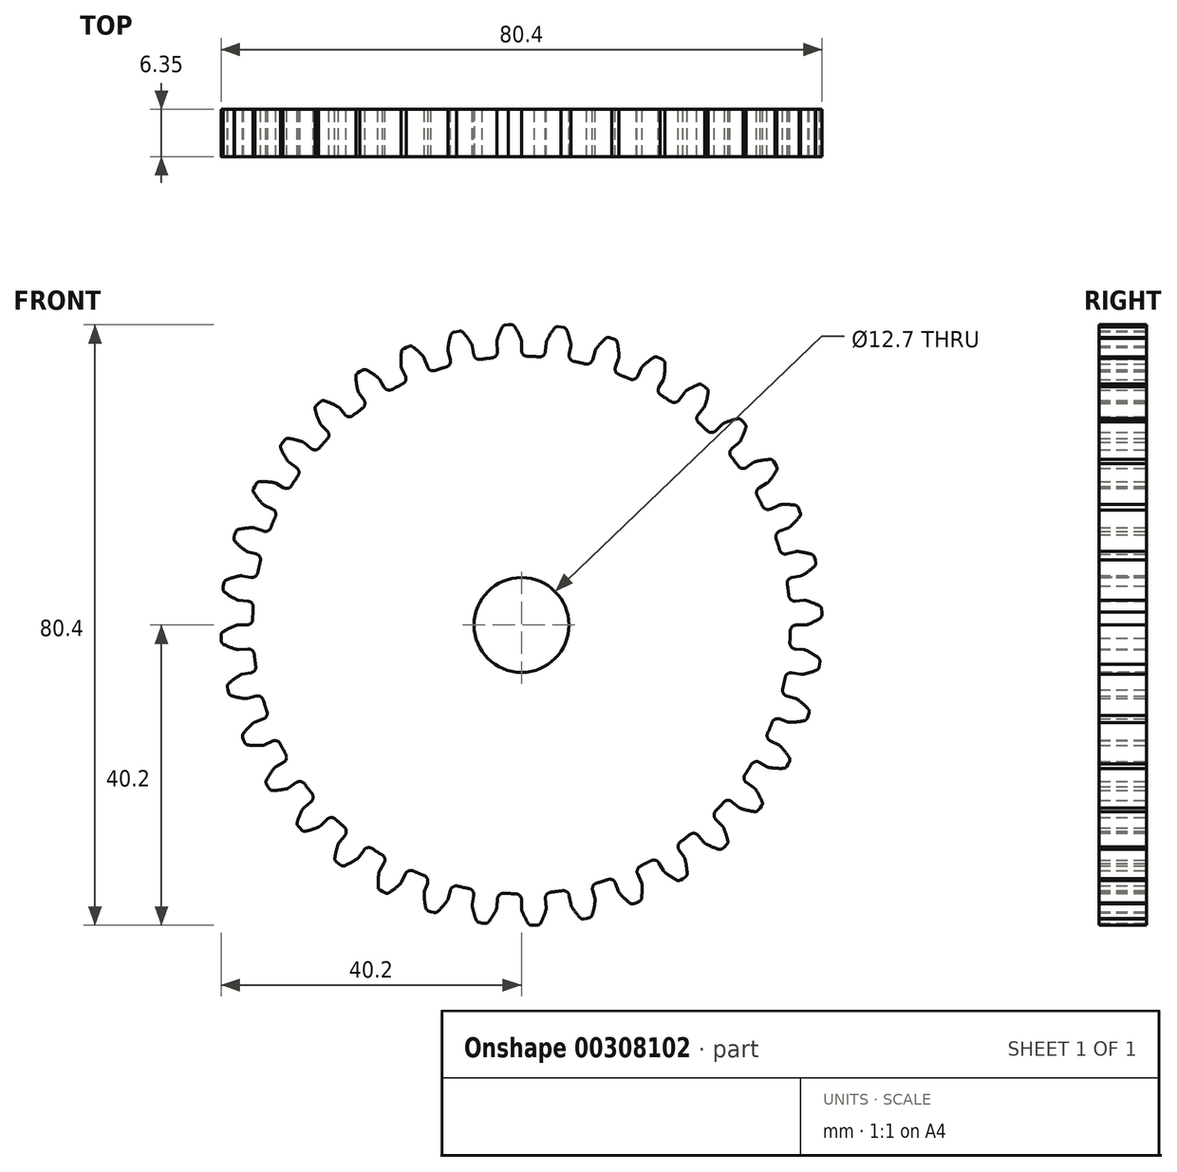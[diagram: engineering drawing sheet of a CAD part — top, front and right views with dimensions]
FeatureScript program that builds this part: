
annotation { "Feature Type Name" : "Feature", "Feature Type Description" : "" }
export const myFeature = defineFeature(function(context is Context, id is Id, definition is map)
    precondition{}
    {
        {
            var Q0;
            Q0=qCreatedBy(makeId("Front.planeOp"),FACE);
            var sketch = newSketch(context, id + "F0", { "sketchPlane" : qUnion([Q0])});
            skArc(sketch, "E0", {"start": v(-3.92, 35.77) * mm, "mid": v(-4.7, 35.68) * mm, "end": v(-5.48, 35.56) * mm});
            skArc(sketch, "E1.trimOffspring", {"start": v(-0.05, 38.24) * mm, "mid": v(-0.44, 39.13) * mm, "end": v(-0.92, 39.97) * mm});
            skLineSegment(sketch, "E2", {"start": v(0, 37.96) * mm, "end": v(0, 36.77) * mm});
            skLineSegment(sketch, "E3", {"start": v(-1.35, 40.2) * mm, "end": v(-1.76, 40.2) * mm});
            skLineSegment(sketch, "E4.MirrorCS", {"start": v(-2.16, 40.17) * mm, "end": v(-1.76, 40.2) * mm});
            skArc(sketch, "E5.MirrorCS", {"start": v(-3.28, 38.1) * mm, "mid": v(-2.97, 39.02) * mm, "end": v(-2.56, 39.9) * mm});
            skLineSegment(sketch, "E6.MirrorCS", {"start": v(-3.3, 37.81) * mm, "end": v(-3.2, 36.63) * mm});
            skPoint(sketch, "E7.visualSharp", {"position": v(-3.14, 35.85) * mm});
            skArc(sketch, "E7.filletArc", {"start": v(-3.92, 35.77) * mm, "mid": v(-3.38, 36.06) * mm, "end": v(-3.2, 36.63) * mm});
            skPoint(sketch, "E8.visualSharp", {"position": v(0, 35.98) * mm});
            skArc(sketch, "E8.filletArc", {"start": v(0, 36.77) * mm, "mid": v(0.23, 36.22) * mm, "end": v(0.78, 35.97) * mm});
            skPoint(sketch, "E9.visualSharp", {"position": v(-3.32, 37.96) * mm});
            skArc(sketch, "E9.filletArc", {"start": v(-3.28, 38.1) * mm, "mid": v(-3.3, 37.96) * mm, "end": v(-3.3, 37.81) * mm});
            skPoint(sketch, "E10.visualSharp", {"position": v(0, 38.1) * mm});
            skArc(sketch, "E10.filletArc", {"start": v(0, 37.96) * mm, "mid": v(-0.01, 38.1) * mm, "end": v(-0.05, 38.24) * mm});
            skPoint(sketch, "E11.visualSharp", {"position": v(-1.08, 40.2) * mm});
            skArc(sketch, "E11.filletArc", {"start": v(-0.92, 39.97) * mm, "mid": v(-1.1, 40.14) * mm, "end": v(-1.35, 40.2) * mm});
            skPoint(sketch, "E12.visualSharp", {"position": v(-2.43, 40.14) * mm});
            skArc(sketch, "E12.filletArc", {"start": v(-2.16, 40.17) * mm, "mid": v(-2.4, 40.08) * mm, "end": v(-2.56, 39.9) * mm});
            skArc(sketch, "E13.1.0", {"start": v(-10.07, 34.55) * mm, "mid": v(-9.6, 34.92) * mm, "end": v(-9.52, 35.52) * mm});
            skLineSegment(sketch, "E13.1.1", {"start": v(-9.82, 36.66) * mm, "end": v(-9.52, 35.52) * mm});
            skArc(sketch, "E13.1.2", {"start": v(-9.85, 36.95) * mm, "mid": v(-9.85, 36.8) * mm, "end": v(-9.82, 36.66) * mm});
            skArc(sketch, "E13.1.3", {"start": v(-9.85, 36.95) * mm, "mid": v(-9.7, 37.9) * mm, "end": v(-9.45, 38.84) * mm});
            skArc(sketch, "E13.1.4", {"start": v(-9.1, 39.18) * mm, "mid": v(-9.32, 39.06) * mm, "end": v(-9.45, 38.84) * mm});
            skLineSegment(sketch, "E13.1.5", {"start": v(-9.1, 39.18) * mm, "end": v(-8.7, 39.29) * mm});
            skLineSegment(sketch, "E13.1.6", {"start": v(-8.31, 39.36) * mm, "end": v(-8.7, 39.29) * mm});
            skArc(sketch, "E13.1.7", {"start": v(-7.85, 39.2) * mm, "mid": v(-8.06, 39.34) * mm, "end": v(-8.31, 39.36) * mm});
            skArc(sketch, "E13.1.8", {"start": v(-6.7, 37.65) * mm, "mid": v(-7.23, 38.46) * mm, "end": v(-7.85, 39.2) * mm});
            skArc(sketch, "E13.1.9", {"start": v(-6.6, 37.38) * mm, "mid": v(-6.63, 37.52) * mm, "end": v(-6.7, 37.65) * mm});
            skLineSegment(sketch, "E13.1.10", {"start": v(-6.6, 37.38) * mm, "end": v(-6.39, 36.22) * mm});
            skArc(sketch, "E13.1.11", {"start": v(-6.39, 36.22) * mm, "mid": v(-6.06, 35.7) * mm, "end": v(-5.48, 35.56) * mm});
            skArc(sketch, "E13.2.0", {"start": v(-15.91, 32.27) * mm, "mid": v(-15.51, 32.73) * mm, "end": v(-15.54, 33.33) * mm});
            skLineSegment(sketch, "E13.2.1", {"start": v(-16.04, 34.4) * mm, "end": v(-15.54, 33.33) * mm});
            skArc(sketch, "E13.2.2", {"start": v(-16.11, 34.68) * mm, "mid": v(-16.1, 34.54) * mm, "end": v(-16.04, 34.4) * mm});
            skArc(sketch, "E13.2.3", {"start": v(-16.11, 34.68) * mm, "mid": v(-16.13, 35.65) * mm, "end": v(-16.05, 36.61) * mm});
            skArc(sketch, "E13.2.4", {"start": v(-15.77, 37) * mm, "mid": v(-15.96, 36.85) * mm, "end": v(-16.05, 36.61) * mm});
            skLineSegment(sketch, "E13.2.5", {"start": v(-15.77, 37) * mm, "end": v(-15.4, 37.18) * mm});
            skLineSegment(sketch, "E13.2.6", {"start": v(-15.02, 37.32) * mm, "end": v(-15.4, 37.18) * mm});
            skArc(sketch, "E13.2.7", {"start": v(-14.54, 37.24) * mm, "mid": v(-14.77, 37.34) * mm, "end": v(-15.02, 37.32) * mm});
            skArc(sketch, "E13.2.8", {"start": v(-13.13, 35.92) * mm, "mid": v(-13.8, 36.62) * mm, "end": v(-14.54, 37.24) * mm});
            skArc(sketch, "E13.2.9", {"start": v(-12.98, 35.67) * mm, "mid": v(-13.04, 35.8) * mm, "end": v(-13.13, 35.92) * mm});
            skLineSegment(sketch, "E13.2.10", {"start": v(-12.98, 35.67) * mm, "end": v(-12.58, 34.56) * mm});
            skArc(sketch, "E13.2.11", {"start": v(-12.58, 34.56) * mm, "mid": v(-12.17, 34.1) * mm, "end": v(-11.57, 34.07) * mm});
            skArc(sketch, "E13.3.0", {"start": v(-21.28, 29.02) * mm, "mid": v(-20.96, 29.53) * mm, "end": v(-21.1, 30.12) * mm});
            skLineSegment(sketch, "E13.3.1", {"start": v(-21.77, 31.1) * mm, "end": v(-21.1, 30.12) * mm});
            skArc(sketch, "E13.3.2", {"start": v(-21.9, 31.36) * mm, "mid": v(-21.84, 31.22) * mm, "end": v(-21.77, 31.1) * mm});
            skArc(sketch, "E13.3.3", {"start": v(-21.9, 31.36) * mm, "mid": v(-22.08, 32.3) * mm, "end": v(-22.17, 33.27) * mm});
            skArc(sketch, "E13.3.4", {"start": v(-21.95, 33.7) * mm, "mid": v(-22.12, 33.52) * mm, "end": v(-22.17, 33.27) * mm});
            skLineSegment(sketch, "E13.3.5", {"start": v(-21.95, 33.7) * mm, "end": v(-21.62, 33.94) * mm});
            skLineSegment(sketch, "E13.3.6", {"start": v(-21.27, 34.14) * mm, "end": v(-21.62, 33.94) * mm});
            skArc(sketch, "E13.3.7", {"start": v(-20.78, 34.15) * mm, "mid": v(-21.03, 34.2) * mm, "end": v(-21.27, 34.14) * mm});
            skArc(sketch, "E13.3.8", {"start": v(-19.17, 33.1) * mm, "mid": v(-19.95, 33.66) * mm, "end": v(-20.78, 34.15) * mm});
            skArc(sketch, "E13.3.9", {"start": v(-18.98, 32.87) * mm, "mid": v(-19.06, 32.99) * mm, "end": v(-19.17, 33.1) * mm});
            skLineSegment(sketch, "E13.3.10", {"start": v(-18.98, 32.87) * mm, "end": v(-18.39, 31.85) * mm});
            skArc(sketch, "E13.3.11", {"start": v(-18.39, 31.85) * mm, "mid": v(-17.9, 31.48) * mm, "end": v(-17.3, 31.55) * mm});
            skArc(sketch, "E13.4.0", {"start": v(-26, 24.88) * mm, "mid": v(-25.77, 25.45) * mm, "end": v(-26, 26) * mm});
            skLineSegment(sketch, "E13.4.1", {"start": v(-26.84, 26.84) * mm, "end": v(-26, 26) * mm});
            skArc(sketch, "E13.4.2", {"start": v(-27, 27.08) * mm, "mid": v(-26.93, 26.95) * mm, "end": v(-26.84, 26.84) * mm});
            skArc(sketch, "E13.4.3", {"start": v(-27, 27.08) * mm, "mid": v(-27.35, 27.98) * mm, "end": v(-27.6, 28.91) * mm});
            skArc(sketch, "E13.4.4", {"start": v(-27.47, 29.38) * mm, "mid": v(-27.6, 29.17) * mm, "end": v(-27.6, 28.91) * mm});
            skLineSegment(sketch, "E13.4.5", {"start": v(-27.47, 29.38) * mm, "end": v(-27.19, 29.67) * mm});
            skLineSegment(sketch, "E13.4.6", {"start": v(-26.88, 29.93) * mm, "end": v(-27.19, 29.67) * mm});
            skArc(sketch, "E13.4.7", {"start": v(-26.4, 30.02) * mm, "mid": v(-26.65, 30.04) * mm, "end": v(-26.88, 29.93) * mm});
            skArc(sketch, "E13.4.8", {"start": v(-24.62, 29.26) * mm, "mid": v(-25.5, 29.69) * mm, "end": v(-26.4, 30.02) * mm});
            skArc(sketch, "E13.4.9", {"start": v(-24.4, 29.08) * mm, "mid": v(-24.5, 29.18) * mm, "end": v(-24.62, 29.26) * mm});
            skLineSegment(sketch, "E13.4.10", {"start": v(-24.4, 29.08) * mm, "end": v(-23.64, 28.17) * mm});
            skArc(sketch, "E13.4.11", {"start": v(-23.64, 28.17) * mm, "mid": v(-23.1, 27.89) * mm, "end": v(-22.52, 28.06) * mm});
            skArc(sketch, "E13.5.0", {"start": v(-29.92, 20) * mm, "mid": v(-29.8, 20.59) * mm, "end": v(-30.12, 21.1) * mm});
            skLineSegment(sketch, "E13.5.1", {"start": v(-31.1, 21.77) * mm, "end": v(-30.12, 21.1) * mm});
            skArc(sketch, "E13.5.2", {"start": v(-31.3, 21.98) * mm, "mid": v(-31.2, 21.86) * mm, "end": v(-31.1, 21.77) * mm});
            skArc(sketch, "E13.5.3", {"start": v(-31.3, 21.98) * mm, "mid": v(-31.8, 22.8) * mm, "end": v(-32.21, 23.68) * mm});
            skArc(sketch, "E13.5.4", {"start": v(-32.16, 24.17) * mm, "mid": v(-32.25, 23.93) * mm, "end": v(-32.21, 23.68) * mm});
            skLineSegment(sketch, "E13.5.5", {"start": v(-32.16, 24.17) * mm, "end": v(-31.92, 24.5) * mm});
            skLineSegment(sketch, "E13.5.6", {"start": v(-31.67, 24.8) * mm, "end": v(-31.92, 24.5) * mm});
            skArc(sketch, "E13.5.7", {"start": v(-31.21, 24.98) * mm, "mid": v(-31.46, 24.95) * mm, "end": v(-31.67, 24.8) * mm});
            skArc(sketch, "E13.5.8", {"start": v(-29.33, 24.54) * mm, "mid": v(-30.26, 24.8) * mm, "end": v(-31.21, 24.98) * mm});
            skArc(sketch, "E13.5.9", {"start": v(-29.08, 24.4) * mm, "mid": v(-29.2, 24.48) * mm, "end": v(-29.33, 24.54) * mm});
            skLineSegment(sketch, "E13.5.10", {"start": v(-29.08, 24.4) * mm, "end": v(-28.17, 23.64) * mm});
            skArc(sketch, "E13.5.11", {"start": v(-28.17, 23.64) * mm, "mid": v(-27.6, 23.45) * mm, "end": v(-27.06, 23.72) * mm});
            skArc(sketch, "E13.6.0", {"start": v(-32.94, 14.5) * mm, "mid": v(-32.92, 15.1) * mm, "end": v(-33.33, 15.54) * mm});
            skLineSegment(sketch, "E13.6.1", {"start": v(-34.4, 16.04) * mm, "end": v(-33.33, 15.54) * mm});
            skArc(sketch, "E13.6.2", {"start": v(-34.64, 16.2) * mm, "mid": v(-34.53, 16.11) * mm, "end": v(-34.4, 16.04) * mm});
            skArc(sketch, "E13.6.3", {"start": v(-34.64, 16.2) * mm, "mid": v(-35.27, 16.94) * mm, "end": v(-35.83, 17.73) * mm});
            skArc(sketch, "E13.6.4", {"start": v(-35.86, 18.22) * mm, "mid": v(-35.91, 17.97) * mm, "end": v(-35.83, 17.73) * mm});
            skLineSegment(sketch, "E13.6.5", {"start": v(-35.86, 18.22) * mm, "end": v(-35.7, 18.58) * mm});
            skLineSegment(sketch, "E13.6.6", {"start": v(-35.5, 18.93) * mm, "end": v(-35.7, 18.58) * mm});
            skArc(sketch, "E13.6.7", {"start": v(-35.07, 19.18) * mm, "mid": v(-35.32, 19.11) * mm, "end": v(-35.5, 18.93) * mm});
            skArc(sketch, "E13.6.8", {"start": v(-33.14, 19.07) * mm, "mid": v(-34.1, 19.18) * mm, "end": v(-35.07, 19.18) * mm});
            skArc(sketch, "E13.6.9", {"start": v(-32.87, 18.98) * mm, "mid": v(-33, 19.04) * mm, "end": v(-33.14, 19.07) * mm});
            skLineSegment(sketch, "E13.6.10", {"start": v(-32.87, 18.98) * mm, "end": v(-31.85, 18.39) * mm});
            skArc(sketch, "E13.6.11", {"start": v(-31.85, 18.39) * mm, "mid": v(-31.25, 18.3) * mm, "end": v(-30.76, 18.67) * mm});
            skArc(sketch, "E13.7.0", {"start": v(-34.95, 8.55) * mm, "mid": v(-35.04, 9.15) * mm, "end": v(-35.52, 9.52) * mm});
            skLineSegment(sketch, "E13.7.1", {"start": v(-36.66, 9.82) * mm, "end": v(-35.52, 9.52) * mm});
            skArc(sketch, "E13.7.2", {"start": v(-36.92, 9.95) * mm, "mid": v(-36.8, 9.87) * mm, "end": v(-36.66, 9.82) * mm});
            skArc(sketch, "E13.7.3", {"start": v(-36.92, 9.95) * mm, "mid": v(-37.68, 10.56) * mm, "end": v(-38.37, 11.24) * mm});
            skArc(sketch, "E13.7.4", {"start": v(-38.48, 11.71) * mm, "mid": v(-38.49, 11.46) * mm, "end": v(-38.37, 11.24) * mm});
            skLineSegment(sketch, "E13.7.5", {"start": v(-38.48, 11.71) * mm, "end": v(-38.38, 12.1) * mm});
            skLineSegment(sketch, "E13.7.6", {"start": v(-38.24, 12.48) * mm, "end": v(-38.38, 12.1) * mm});
            skArc(sketch, "E13.7.7", {"start": v(-37.87, 12.8) * mm, "mid": v(-38.1, 12.69) * mm, "end": v(-38.24, 12.48) * mm});
            skArc(sketch, "E13.7.8", {"start": v(-35.95, 13.03) * mm, "mid": v(-36.92, 12.96) * mm, "end": v(-37.87, 12.8) * mm});
            skArc(sketch, "E13.7.9", {"start": v(-35.67, 12.98) * mm, "mid": v(-35.8, 13.02) * mm, "end": v(-35.95, 13.03) * mm});
            skLineSegment(sketch, "E13.7.10", {"start": v(-35.67, 12.98) * mm, "end": v(-34.56, 12.58) * mm});
            skArc(sketch, "E13.7.11", {"start": v(-34.56, 12.58) * mm, "mid": v(-33.95, 12.6) * mm, "end": v(-33.54, 13.04) * mm});
            skArc(sketch, "E13.8.0", {"start": v(-35.9, 2.36) * mm, "mid": v(-36.1, 2.93) * mm, "end": v(-36.63, 3.2) * mm});
            skLineSegment(sketch, "E13.8.1", {"start": v(-37.81, 3.3) * mm, "end": v(-36.63, 3.2) * mm});
            skArc(sketch, "E13.8.2", {"start": v(-38.1, 3.39) * mm, "mid": v(-37.95, 3.33) * mm, "end": v(-37.81, 3.3) * mm});
            skArc(sketch, "E13.8.3", {"start": v(-38.1, 3.39) * mm, "mid": v(-38.94, 3.85) * mm, "end": v(-39.74, 4.4) * mm});
            skArc(sketch, "E13.8.4", {"start": v(-39.93, 4.85) * mm, "mid": v(-39.9, 4.6) * mm, "end": v(-39.74, 4.4) * mm});
            skLineSegment(sketch, "E13.8.5", {"start": v(-39.93, 4.85) * mm, "end": v(-39.9, 5.25) * mm});
            skLineSegment(sketch, "E13.8.6", {"start": v(-39.83, 5.65) * mm, "end": v(-39.9, 5.25) * mm});
            skArc(sketch, "E13.8.7", {"start": v(-39.52, 6.03) * mm, "mid": v(-39.72, 5.88) * mm, "end": v(-39.83, 5.65) * mm});
            skArc(sketch, "E13.8.8", {"start": v(-37.67, 6.59) * mm, "mid": v(-38.6, 6.36) * mm, "end": v(-39.52, 6.03) * mm});
            skArc(sketch, "E13.8.9", {"start": v(-37.38, 6.6) * mm, "mid": v(-37.52, 6.6) * mm, "end": v(-37.67, 6.59) * mm});
            skLineSegment(sketch, "E13.8.10", {"start": v(-37.38, 6.6) * mm, "end": v(-36.22, 6.39) * mm});
            skArc(sketch, "E13.8.11", {"start": v(-36.22, 6.39) * mm, "mid": v(-35.63, 6.51) * mm, "end": v(-35.3, 7.02) * mm});
            skArc(sketch, "E13.9.0", {"start": v(-35.77, -3.92) * mm, "mid": v(-36.06, -3.38) * mm, "end": v(-36.63, -3.2) * mm});
            skLineSegment(sketch, "E13.9.1", {"start": v(-37.81, -3.3) * mm, "end": v(-36.63, -3.2) * mm});
            skArc(sketch, "E13.9.2", {"start": v(-38.1, -3.28) * mm, "mid": v(-37.96, -3.3) * mm, "end": v(-37.81, -3.3) * mm});
            skArc(sketch, "E13.9.3", {"start": v(-38.1, -3.28) * mm, "mid": v(-39.02, -2.97) * mm, "end": v(-39.9, -2.56) * mm});
            skArc(sketch, "E13.9.4", {"start": v(-40.17, -2.16) * mm, "mid": v(-40.08, -2.4) * mm, "end": v(-39.9, -2.56) * mm});
            skLineSegment(sketch, "E13.9.5", {"start": v(-40.17, -2.16) * mm, "end": v(-40.2, -1.76) * mm});
            skLineSegment(sketch, "E13.9.6", {"start": v(-40.2, -1.35) * mm, "end": v(-40.2, -1.76) * mm});
            skArc(sketch, "E13.9.7", {"start": v(-39.97, -0.92) * mm, "mid": v(-40.14, -1.1) * mm, "end": v(-40.2, -1.35) * mm});
            skArc(sketch, "E13.9.8", {"start": v(-38.24, -0.05) * mm, "mid": v(-39.13, -0.44) * mm, "end": v(-39.97, -0.92) * mm});
            skArc(sketch, "E13.9.9", {"start": v(-37.96, 0) * mm, "mid": v(-38.1, -0.01) * mm, "end": v(-38.24, -0.05) * mm});
            skLineSegment(sketch, "E13.9.10", {"start": v(-37.96, 0) * mm, "end": v(-36.77, 0) * mm});
            skArc(sketch, "E13.9.11", {"start": v(-36.77, 0) * mm, "mid": v(-36.22, 0.23) * mm, "end": v(-35.97, 0.78) * mm});
            skArc(sketch, "E13.10.0", {"start": v(-34.55, -10.07) * mm, "mid": v(-34.92, -9.6) * mm, "end": v(-35.52, -9.52) * mm});
            skLineSegment(sketch, "E13.10.1", {"start": v(-36.66, -9.82) * mm, "end": v(-35.52, -9.52) * mm});
            skArc(sketch, "E13.10.2", {"start": v(-36.95, -9.85) * mm, "mid": v(-36.8, -9.85) * mm, "end": v(-36.66, -9.82) * mm});
            skArc(sketch, "E13.10.3", {"start": v(-36.95, -9.85) * mm, "mid": v(-37.9, -9.7) * mm, "end": v(-38.84, -9.45) * mm});
            skArc(sketch, "E13.10.4", {"start": v(-39.18, -9.1) * mm, "mid": v(-39.06, -9.32) * mm, "end": v(-38.84, -9.45) * mm});
            skLineSegment(sketch, "E13.10.5", {"start": v(-39.18, -9.1) * mm, "end": v(-39.29, -8.7) * mm});
            skLineSegment(sketch, "E13.10.6", {"start": v(-39.36, -8.31) * mm, "end": v(-39.29, -8.7) * mm});
            skArc(sketch, "E13.10.7", {"start": v(-39.2, -7.85) * mm, "mid": v(-39.34, -8.06) * mm, "end": v(-39.36, -8.31) * mm});
            skArc(sketch, "E13.10.8", {"start": v(-37.65, -6.7) * mm, "mid": v(-38.46, -7.23) * mm, "end": v(-39.2, -7.85) * mm});
            skArc(sketch, "E13.10.9", {"start": v(-37.38, -6.6) * mm, "mid": v(-37.52, -6.63) * mm, "end": v(-37.65, -6.7) * mm});
            skLineSegment(sketch, "E13.10.10", {"start": v(-37.38, -6.6) * mm, "end": v(-36.22, -6.39) * mm});
            skArc(sketch, "E13.10.11", {"start": v(-36.22, -6.39) * mm, "mid": v(-35.7, -6.06) * mm, "end": v(-35.56, -5.48) * mm});
            skArc(sketch, "E13.11.0", {"start": v(-32.27, -15.91) * mm, "mid": v(-32.73, -15.51) * mm, "end": v(-33.33, -15.54) * mm});
            skLineSegment(sketch, "E13.11.1", {"start": v(-34.4, -16.04) * mm, "end": v(-33.33, -15.54) * mm});
            skArc(sketch, "E13.11.2", {"start": v(-34.68, -16.11) * mm, "mid": v(-34.54, -16.1) * mm, "end": v(-34.4, -16.04) * mm});
            skArc(sketch, "E13.11.3", {"start": v(-34.68, -16.11) * mm, "mid": v(-35.65, -16.13) * mm, "end": v(-36.61, -16.05) * mm});
            skArc(sketch, "E13.11.4", {"start": v(-37, -15.77) * mm, "mid": v(-36.85, -15.96) * mm, "end": v(-36.61, -16.05) * mm});
            skLineSegment(sketch, "E13.11.5", {"start": v(-37, -15.77) * mm, "end": v(-37.18, -15.4) * mm});
            skLineSegment(sketch, "E13.11.6", {"start": v(-37.32, -15.02) * mm, "end": v(-37.18, -15.4) * mm});
            skArc(sketch, "E13.11.7", {"start": v(-37.24, -14.54) * mm, "mid": v(-37.34, -14.77) * mm, "end": v(-37.32, -15.02) * mm});
            skArc(sketch, "E13.11.8", {"start": v(-35.92, -13.13) * mm, "mid": v(-36.62, -13.8) * mm, "end": v(-37.24, -14.54) * mm});
            skArc(sketch, "E13.11.9", {"start": v(-35.67, -12.98) * mm, "mid": v(-35.8, -13.04) * mm, "end": v(-35.92, -13.13) * mm});
            skLineSegment(sketch, "E13.11.10", {"start": v(-35.67, -12.98) * mm, "end": v(-34.56, -12.58) * mm});
            skArc(sketch, "E13.11.11", {"start": v(-34.56, -12.58) * mm, "mid": v(-34.1, -12.17) * mm, "end": v(-34.07, -11.57) * mm});
            skArc(sketch, "E13.12.0", {"start": v(-29.02, -21.28) * mm, "mid": v(-29.53, -20.96) * mm, "end": v(-30.12, -21.1) * mm});
            skLineSegment(sketch, "E13.12.1", {"start": v(-31.1, -21.77) * mm, "end": v(-30.12, -21.1) * mm});
            skArc(sketch, "E13.12.2", {"start": v(-31.36, -21.9) * mm, "mid": v(-31.22, -21.84) * mm, "end": v(-31.1, -21.77) * mm});
            skArc(sketch, "E13.12.3", {"start": v(-31.36, -21.9) * mm, "mid": v(-32.3, -22.08) * mm, "end": v(-33.27, -22.17) * mm});
            skArc(sketch, "E13.12.4", {"start": v(-33.7, -21.95) * mm, "mid": v(-33.52, -22.12) * mm, "end": v(-33.27, -22.17) * mm});
            skLineSegment(sketch, "E13.12.5", {"start": v(-33.7, -21.95) * mm, "end": v(-33.94, -21.62) * mm});
            skLineSegment(sketch, "E13.12.6", {"start": v(-34.14, -21.27) * mm, "end": v(-33.94, -21.62) * mm});
            skArc(sketch, "E13.12.7", {"start": v(-34.15, -20.78) * mm, "mid": v(-34.2, -21.03) * mm, "end": v(-34.14, -21.27) * mm});
            skArc(sketch, "E13.12.8", {"start": v(-33.1, -19.17) * mm, "mid": v(-33.66, -19.95) * mm, "end": v(-34.15, -20.78) * mm});
            skArc(sketch, "E13.12.9", {"start": v(-32.87, -18.98) * mm, "mid": v(-32.99, -19.06) * mm, "end": v(-33.1, -19.17) * mm});
            skLineSegment(sketch, "E13.12.10", {"start": v(-32.87, -18.98) * mm, "end": v(-31.85, -18.39) * mm});
            skArc(sketch, "E13.12.11", {"start": v(-31.85, -18.39) * mm, "mid": v(-31.48, -17.9) * mm, "end": v(-31.55, -17.3) * mm});
            skArc(sketch, "E13.13.0", {"start": v(-24.88, -26) * mm, "mid": v(-25.45, -25.77) * mm, "end": v(-26, -26) * mm});
            skLineSegment(sketch, "E13.13.1", {"start": v(-26.84, -26.84) * mm, "end": v(-26, -26) * mm});
            skArc(sketch, "E13.13.2", {"start": v(-27.08, -27) * mm, "mid": v(-26.95, -26.93) * mm, "end": v(-26.84, -26.84) * mm});
            skArc(sketch, "E13.13.3", {"start": v(-27.08, -27) * mm, "mid": v(-27.98, -27.35) * mm, "end": v(-28.91, -27.6) * mm});
            skArc(sketch, "E13.13.4", {"start": v(-29.38, -27.47) * mm, "mid": v(-29.17, -27.6) * mm, "end": v(-28.91, -27.6) * mm});
            skLineSegment(sketch, "E13.13.5", {"start": v(-29.38, -27.47) * mm, "end": v(-29.67, -27.19) * mm});
            skLineSegment(sketch, "E13.13.6", {"start": v(-29.93, -26.88) * mm, "end": v(-29.67, -27.19) * mm});
            skArc(sketch, "E13.13.7", {"start": v(-30.02, -26.4) * mm, "mid": v(-30.04, -26.65) * mm, "end": v(-29.93, -26.88) * mm});
            skArc(sketch, "E13.13.8", {"start": v(-29.26, -24.62) * mm, "mid": v(-29.69, -25.5) * mm, "end": v(-30.02, -26.4) * mm});
            skArc(sketch, "E13.13.9", {"start": v(-29.08, -24.4) * mm, "mid": v(-29.18, -24.5) * mm, "end": v(-29.26, -24.62) * mm});
            skLineSegment(sketch, "E13.13.10", {"start": v(-29.08, -24.4) * mm, "end": v(-28.17, -23.64) * mm});
            skArc(sketch, "E13.13.11", {"start": v(-28.17, -23.64) * mm, "mid": v(-27.89, -23.1) * mm, "end": v(-28.06, -22.52) * mm});
            skArc(sketch, "E13.14.0", {"start": v(-20, -29.92) * mm, "mid": v(-20.59, -29.8) * mm, "end": v(-21.1, -30.12) * mm});
            skLineSegment(sketch, "E13.14.1", {"start": v(-21.77, -31.1) * mm, "end": v(-21.1, -30.12) * mm});
            skArc(sketch, "E13.14.2", {"start": v(-21.98, -31.3) * mm, "mid": v(-21.86, -31.2) * mm, "end": v(-21.77, -31.1) * mm});
            skArc(sketch, "E13.14.3", {"start": v(-21.98, -31.3) * mm, "mid": v(-22.8, -31.8) * mm, "end": v(-23.68, -32.21) * mm});
            skArc(sketch, "E13.14.4", {"start": v(-24.17, -32.16) * mm, "mid": v(-23.93, -32.25) * mm, "end": v(-23.68, -32.21) * mm});
            skLineSegment(sketch, "E13.14.5", {"start": v(-24.17, -32.16) * mm, "end": v(-24.5, -31.92) * mm});
            skLineSegment(sketch, "E13.14.6", {"start": v(-24.8, -31.67) * mm, "end": v(-24.5, -31.92) * mm});
            skArc(sketch, "E13.14.7", {"start": v(-24.98, -31.21) * mm, "mid": v(-24.95, -31.46) * mm, "end": v(-24.8, -31.67) * mm});
            skArc(sketch, "E13.14.8", {"start": v(-24.54, -29.33) * mm, "mid": v(-24.8, -30.26) * mm, "end": v(-24.98, -31.21) * mm});
            skArc(sketch, "E13.14.9", {"start": v(-24.4, -29.08) * mm, "mid": v(-24.48, -29.2) * mm, "end": v(-24.54, -29.33) * mm});
            skLineSegment(sketch, "E13.14.10", {"start": v(-24.4, -29.08) * mm, "end": v(-23.64, -28.17) * mm});
            skArc(sketch, "E13.14.11", {"start": v(-23.64, -28.17) * mm, "mid": v(-23.45, -27.6) * mm, "end": v(-23.72, -27.06) * mm});
            skArc(sketch, "E13.15.0", {"start": v(-14.5, -32.94) * mm, "mid": v(-15.1, -32.92) * mm, "end": v(-15.54, -33.33) * mm});
            skLineSegment(sketch, "E13.15.1", {"start": v(-16.04, -34.4) * mm, "end": v(-15.54, -33.33) * mm});
            skArc(sketch, "E13.15.2", {"start": v(-16.2, -34.64) * mm, "mid": v(-16.11, -34.53) * mm, "end": v(-16.04, -34.4) * mm});
            skArc(sketch, "E13.15.3", {"start": v(-16.2, -34.64) * mm, "mid": v(-16.94, -35.27) * mm, "end": v(-17.73, -35.83) * mm});
            skArc(sketch, "E13.15.4", {"start": v(-18.22, -35.86) * mm, "mid": v(-17.97, -35.91) * mm, "end": v(-17.73, -35.83) * mm});
            skLineSegment(sketch, "E13.15.5", {"start": v(-18.22, -35.86) * mm, "end": v(-18.58, -35.7) * mm});
            skLineSegment(sketch, "E13.15.6", {"start": v(-18.93, -35.5) * mm, "end": v(-18.58, -35.7) * mm});
            skArc(sketch, "E13.15.7", {"start": v(-19.18, -35.07) * mm, "mid": v(-19.11, -35.32) * mm, "end": v(-18.93, -35.5) * mm});
            skArc(sketch, "E13.15.8", {"start": v(-19.07, -33.14) * mm, "mid": v(-19.18, -34.1) * mm, "end": v(-19.18, -35.07) * mm});
            skArc(sketch, "E13.15.9", {"start": v(-18.98, -32.87) * mm, "mid": v(-19.04, -33) * mm, "end": v(-19.07, -33.14) * mm});
            skLineSegment(sketch, "E13.15.10", {"start": v(-18.98, -32.87) * mm, "end": v(-18.39, -31.85) * mm});
            skArc(sketch, "E13.15.11", {"start": v(-18.39, -31.85) * mm, "mid": v(-18.3, -31.25) * mm, "end": v(-18.67, -30.76) * mm});
            skArc(sketch, "E13.16.0", {"start": v(-8.55, -34.95) * mm, "mid": v(-9.15, -35.04) * mm, "end": v(-9.52, -35.52) * mm});
            skLineSegment(sketch, "E13.16.1", {"start": v(-9.82, -36.66) * mm, "end": v(-9.52, -35.52) * mm});
            skArc(sketch, "E13.16.2", {"start": v(-9.95, -36.92) * mm, "mid": v(-9.87, -36.8) * mm, "end": v(-9.82, -36.66) * mm});
            skArc(sketch, "E13.16.3", {"start": v(-9.95, -36.92) * mm, "mid": v(-10.56, -37.68) * mm, "end": v(-11.24, -38.37) * mm});
            skArc(sketch, "E13.16.4", {"start": v(-11.71, -38.48) * mm, "mid": v(-11.46, -38.49) * mm, "end": v(-11.24, -38.37) * mm});
            skLineSegment(sketch, "E13.16.5", {"start": v(-11.71, -38.48) * mm, "end": v(-12.1, -38.38) * mm});
            skLineSegment(sketch, "E13.16.6", {"start": v(-12.48, -38.24) * mm, "end": v(-12.1, -38.38) * mm});
            skArc(sketch, "E13.16.7", {"start": v(-12.8, -37.87) * mm, "mid": v(-12.69, -38.1) * mm, "end": v(-12.48, -38.24) * mm});
            skArc(sketch, "E13.16.8", {"start": v(-13.03, -35.95) * mm, "mid": v(-12.96, -36.92) * mm, "end": v(-12.8, -37.87) * mm});
            skArc(sketch, "E13.16.9", {"start": v(-12.98, -35.67) * mm, "mid": v(-13.02, -35.8) * mm, "end": v(-13.03, -35.95) * mm});
            skLineSegment(sketch, "E13.16.10", {"start": v(-12.98, -35.67) * mm, "end": v(-12.58, -34.56) * mm});
            skArc(sketch, "E13.16.11", {"start": v(-12.58, -34.56) * mm, "mid": v(-12.6, -33.95) * mm, "end": v(-13.04, -33.54) * mm});
            skArc(sketch, "E13.17.0", {"start": v(-2.36, -35.9) * mm, "mid": v(-2.93, -36.1) * mm, "end": v(-3.2, -36.63) * mm});
            skLineSegment(sketch, "E13.17.1", {"start": v(-3.3, -37.81) * mm, "end": v(-3.2, -36.63) * mm});
            skArc(sketch, "E13.17.2", {"start": v(-3.39, -38.1) * mm, "mid": v(-3.33, -37.95) * mm, "end": v(-3.3, -37.81) * mm});
            skArc(sketch, "E13.17.3", {"start": v(-3.39, -38.1) * mm, "mid": v(-3.85, -38.94) * mm, "end": v(-4.4, -39.74) * mm});
            skArc(sketch, "E13.17.4", {"start": v(-4.85, -39.93) * mm, "mid": v(-4.6, -39.9) * mm, "end": v(-4.4, -39.74) * mm});
            skLineSegment(sketch, "E13.17.5", {"start": v(-4.85, -39.93) * mm, "end": v(-5.25, -39.9) * mm});
            skLineSegment(sketch, "E13.17.6", {"start": v(-5.65, -39.83) * mm, "end": v(-5.25, -39.9) * mm});
            skArc(sketch, "E13.17.7", {"start": v(-6.03, -39.52) * mm, "mid": v(-5.88, -39.72) * mm, "end": v(-5.65, -39.83) * mm});
            skArc(sketch, "E13.17.8", {"start": v(-6.59, -37.67) * mm, "mid": v(-6.36, -38.6) * mm, "end": v(-6.03, -39.52) * mm});
            skArc(sketch, "E13.17.9", {"start": v(-6.6, -37.38) * mm, "mid": v(-6.6, -37.52) * mm, "end": v(-6.59, -37.67) * mm});
            skLineSegment(sketch, "E13.17.10", {"start": v(-6.6, -37.38) * mm, "end": v(-6.39, -36.22) * mm});
            skArc(sketch, "E13.17.11", {"start": v(-6.39, -36.22) * mm, "mid": v(-6.51, -35.63) * mm, "end": v(-7.02, -35.3) * mm});
            skArc(sketch, "E13.18.0", {"start": v(3.92, -35.77) * mm, "mid": v(3.38, -36.06) * mm, "end": v(3.2, -36.63) * mm});
            skLineSegment(sketch, "E13.18.1", {"start": v(3.3, -37.81) * mm, "end": v(3.2, -36.63) * mm});
            skArc(sketch, "E13.18.2", {"start": v(3.28, -38.1) * mm, "mid": v(3.3, -37.96) * mm, "end": v(3.3, -37.81) * mm});
            skArc(sketch, "E13.18.3", {"start": v(3.28, -38.1) * mm, "mid": v(2.97, -39.02) * mm, "end": v(2.56, -39.9) * mm});
            skArc(sketch, "E13.18.4", {"start": v(2.16, -40.17) * mm, "mid": v(2.4, -40.08) * mm, "end": v(2.56, -39.9) * mm});
            skLineSegment(sketch, "E13.18.5", {"start": v(2.16, -40.17) * mm, "end": v(1.76, -40.2) * mm});
            skLineSegment(sketch, "E13.18.6", {"start": v(1.35, -40.2) * mm, "end": v(1.76, -40.2) * mm});
            skArc(sketch, "E13.18.7", {"start": v(0.92, -39.97) * mm, "mid": v(1.1, -40.14) * mm, "end": v(1.35, -40.2) * mm});
            skArc(sketch, "E13.18.8", {"start": v(0.05, -38.24) * mm, "mid": v(0.44, -39.13) * mm, "end": v(0.92, -39.97) * mm});
            skArc(sketch, "E13.18.9", {"start": v(0, -37.96) * mm, "mid": v(0.01, -38.1) * mm, "end": v(0.05, -38.24) * mm});
            skLineSegment(sketch, "E13.18.10", {"start": v(0, -37.96) * mm, "end": v(0, -36.77) * mm});
            skArc(sketch, "E13.18.11", {"start": v(0, -36.77) * mm, "mid": v(-0.23, -36.22) * mm, "end": v(-0.78, -35.97) * mm});
            skArc(sketch, "E13.19.0", {"start": v(10.07, -34.55) * mm, "mid": v(9.6, -34.92) * mm, "end": v(9.52, -35.52) * mm});
            skLineSegment(sketch, "E13.19.1", {"start": v(9.82, -36.66) * mm, "end": v(9.52, -35.52) * mm});
            skArc(sketch, "E13.19.2", {"start": v(9.85, -36.95) * mm, "mid": v(9.85, -36.8) * mm, "end": v(9.82, -36.66) * mm});
            skArc(sketch, "E13.19.3", {"start": v(9.85, -36.95) * mm, "mid": v(9.7, -37.9) * mm, "end": v(9.45, -38.84) * mm});
            skArc(sketch, "E13.19.4", {"start": v(9.1, -39.18) * mm, "mid": v(9.32, -39.06) * mm, "end": v(9.45, -38.84) * mm});
            skLineSegment(sketch, "E13.19.5", {"start": v(9.1, -39.18) * mm, "end": v(8.7, -39.29) * mm});
            skLineSegment(sketch, "E13.19.6", {"start": v(8.31, -39.36) * mm, "end": v(8.7, -39.29) * mm});
            skArc(sketch, "E13.19.7", {"start": v(7.85, -39.2) * mm, "mid": v(8.06, -39.34) * mm, "end": v(8.31, -39.36) * mm});
            skArc(sketch, "E13.19.8", {"start": v(6.7, -37.65) * mm, "mid": v(7.23, -38.46) * mm, "end": v(7.85, -39.2) * mm});
            skArc(sketch, "E13.19.9", {"start": v(6.6, -37.38) * mm, "mid": v(6.63, -37.52) * mm, "end": v(6.7, -37.65) * mm});
            skLineSegment(sketch, "E13.19.10", {"start": v(6.6, -37.38) * mm, "end": v(6.39, -36.22) * mm});
            skArc(sketch, "E13.19.11", {"start": v(6.39, -36.22) * mm, "mid": v(6.06, -35.7) * mm, "end": v(5.48, -35.56) * mm});
            skArc(sketch, "E13.20.0", {"start": v(15.91, -32.27) * mm, "mid": v(15.51, -32.73) * mm, "end": v(15.54, -33.33) * mm});
            skLineSegment(sketch, "E13.20.1", {"start": v(16.04, -34.4) * mm, "end": v(15.54, -33.33) * mm});
            skArc(sketch, "E13.20.2", {"start": v(16.11, -34.68) * mm, "mid": v(16.1, -34.54) * mm, "end": v(16.04, -34.4) * mm});
            skArc(sketch, "E13.20.3", {"start": v(16.11, -34.68) * mm, "mid": v(16.13, -35.65) * mm, "end": v(16.05, -36.61) * mm});
            skArc(sketch, "E13.20.4", {"start": v(15.77, -37) * mm, "mid": v(15.96, -36.85) * mm, "end": v(16.05, -36.61) * mm});
            skLineSegment(sketch, "E13.20.5", {"start": v(15.77, -37) * mm, "end": v(15.4, -37.18) * mm});
            skLineSegment(sketch, "E13.20.6", {"start": v(15.02, -37.32) * mm, "end": v(15.4, -37.18) * mm});
            skArc(sketch, "E13.20.7", {"start": v(14.54, -37.24) * mm, "mid": v(14.77, -37.34) * mm, "end": v(15.02, -37.32) * mm});
            skArc(sketch, "E13.20.8", {"start": v(13.13, -35.92) * mm, "mid": v(13.8, -36.62) * mm, "end": v(14.54, -37.24) * mm});
            skArc(sketch, "E13.20.9", {"start": v(12.98, -35.67) * mm, "mid": v(13.04, -35.8) * mm, "end": v(13.13, -35.92) * mm});
            skLineSegment(sketch, "E13.20.10", {"start": v(12.98, -35.67) * mm, "end": v(12.58, -34.56) * mm});
            skArc(sketch, "E13.20.11", {"start": v(12.58, -34.56) * mm, "mid": v(12.17, -34.1) * mm, "end": v(11.57, -34.07) * mm});
            skArc(sketch, "E13.21.0", {"start": v(21.28, -29.02) * mm, "mid": v(20.96, -29.53) * mm, "end": v(21.1, -30.12) * mm});
            skLineSegment(sketch, "E13.21.1", {"start": v(21.77, -31.1) * mm, "end": v(21.1, -30.12) * mm});
            skArc(sketch, "E13.21.2", {"start": v(21.9, -31.36) * mm, "mid": v(21.84, -31.22) * mm, "end": v(21.77, -31.1) * mm});
            skArc(sketch, "E13.21.3", {"start": v(21.9, -31.36) * mm, "mid": v(22.08, -32.3) * mm, "end": v(22.17, -33.27) * mm});
            skArc(sketch, "E13.21.4", {"start": v(21.95, -33.7) * mm, "mid": v(22.12, -33.52) * mm, "end": v(22.17, -33.27) * mm});
            skLineSegment(sketch, "E13.21.5", {"start": v(21.95, -33.7) * mm, "end": v(21.62, -33.94) * mm});
            skLineSegment(sketch, "E13.21.6", {"start": v(21.27, -34.14) * mm, "end": v(21.62, -33.94) * mm});
            skArc(sketch, "E13.21.7", {"start": v(20.78, -34.15) * mm, "mid": v(21.03, -34.2) * mm, "end": v(21.27, -34.14) * mm});
            skArc(sketch, "E13.21.8", {"start": v(19.17, -33.1) * mm, "mid": v(19.95, -33.66) * mm, "end": v(20.78, -34.15) * mm});
            skArc(sketch, "E13.21.9", {"start": v(18.98, -32.87) * mm, "mid": v(19.06, -32.99) * mm, "end": v(19.17, -33.1) * mm});
            skLineSegment(sketch, "E13.21.10", {"start": v(18.98, -32.87) * mm, "end": v(18.39, -31.85) * mm});
            skArc(sketch, "E13.21.11", {"start": v(18.39, -31.85) * mm, "mid": v(17.9, -31.48) * mm, "end": v(17.3, -31.55) * mm});
            skArc(sketch, "E13.22.0", {"start": v(26, -24.88) * mm, "mid": v(25.77, -25.45) * mm, "end": v(26, -26) * mm});
            skLineSegment(sketch, "E13.22.1", {"start": v(26.84, -26.84) * mm, "end": v(26, -26) * mm});
            skArc(sketch, "E13.22.2", {"start": v(27, -27.08) * mm, "mid": v(26.93, -26.95) * mm, "end": v(26.84, -26.84) * mm});
            skArc(sketch, "E13.22.3", {"start": v(27, -27.08) * mm, "mid": v(27.35, -27.98) * mm, "end": v(27.6, -28.91) * mm});
            skArc(sketch, "E13.22.4", {"start": v(27.47, -29.38) * mm, "mid": v(27.6, -29.17) * mm, "end": v(27.6, -28.91) * mm});
            skLineSegment(sketch, "E13.22.5", {"start": v(27.47, -29.38) * mm, "end": v(27.19, -29.67) * mm});
            skLineSegment(sketch, "E13.22.6", {"start": v(26.88, -29.93) * mm, "end": v(27.19, -29.67) * mm});
            skArc(sketch, "E13.22.7", {"start": v(26.4, -30.02) * mm, "mid": v(26.65, -30.04) * mm, "end": v(26.88, -29.93) * mm});
            skArc(sketch, "E13.22.8", {"start": v(24.62, -29.26) * mm, "mid": v(25.5, -29.69) * mm, "end": v(26.4, -30.02) * mm});
            skArc(sketch, "E13.22.9", {"start": v(24.4, -29.08) * mm, "mid": v(24.5, -29.18) * mm, "end": v(24.62, -29.26) * mm});
            skLineSegment(sketch, "E13.22.10", {"start": v(24.4, -29.08) * mm, "end": v(23.64, -28.17) * mm});
            skArc(sketch, "E13.22.11", {"start": v(23.64, -28.17) * mm, "mid": v(23.1, -27.89) * mm, "end": v(22.52, -28.06) * mm});
            skArc(sketch, "E13.23.0", {"start": v(29.92, -20) * mm, "mid": v(29.8, -20.59) * mm, "end": v(30.12, -21.1) * mm});
            skLineSegment(sketch, "E13.23.1", {"start": v(31.1, -21.77) * mm, "end": v(30.12, -21.1) * mm});
            skArc(sketch, "E13.23.2", {"start": v(31.3, -21.98) * mm, "mid": v(31.2, -21.86) * mm, "end": v(31.1, -21.77) * mm});
            skArc(sketch, "E13.23.3", {"start": v(31.3, -21.98) * mm, "mid": v(31.8, -22.8) * mm, "end": v(32.21, -23.68) * mm});
            skArc(sketch, "E13.23.4", {"start": v(32.16, -24.17) * mm, "mid": v(32.25, -23.93) * mm, "end": v(32.21, -23.68) * mm});
            skLineSegment(sketch, "E13.23.5", {"start": v(32.16, -24.17) * mm, "end": v(31.92, -24.5) * mm});
            skLineSegment(sketch, "E13.23.6", {"start": v(31.67, -24.8) * mm, "end": v(31.92, -24.5) * mm});
            skArc(sketch, "E13.23.7", {"start": v(31.21, -24.98) * mm, "mid": v(31.46, -24.95) * mm, "end": v(31.67, -24.8) * mm});
            skArc(sketch, "E13.23.8", {"start": v(29.33, -24.54) * mm, "mid": v(30.26, -24.8) * mm, "end": v(31.21, -24.98) * mm});
            skArc(sketch, "E13.23.9", {"start": v(29.08, -24.4) * mm, "mid": v(29.2, -24.48) * mm, "end": v(29.33, -24.54) * mm});
            skLineSegment(sketch, "E13.23.10", {"start": v(29.08, -24.4) * mm, "end": v(28.17, -23.64) * mm});
            skArc(sketch, "E13.23.11", {"start": v(28.17, -23.64) * mm, "mid": v(27.6, -23.45) * mm, "end": v(27.06, -23.72) * mm});
            skArc(sketch, "E13.24.0", {"start": v(32.94, -14.5) * mm, "mid": v(32.92, -15.1) * mm, "end": v(33.33, -15.54) * mm});
            skLineSegment(sketch, "E13.24.1", {"start": v(34.4, -16.04) * mm, "end": v(33.33, -15.54) * mm});
            skArc(sketch, "E13.24.2", {"start": v(34.64, -16.2) * mm, "mid": v(34.53, -16.11) * mm, "end": v(34.4, -16.04) * mm});
            skArc(sketch, "E13.24.3", {"start": v(34.64, -16.2) * mm, "mid": v(35.27, -16.94) * mm, "end": v(35.83, -17.73) * mm});
            skArc(sketch, "E13.24.4", {"start": v(35.86, -18.22) * mm, "mid": v(35.91, -17.97) * mm, "end": v(35.83, -17.73) * mm});
            skLineSegment(sketch, "E13.24.5", {"start": v(35.86, -18.22) * mm, "end": v(35.7, -18.58) * mm});
            skLineSegment(sketch, "E13.24.6", {"start": v(35.5, -18.93) * mm, "end": v(35.7, -18.58) * mm});
            skArc(sketch, "E13.24.7", {"start": v(35.07, -19.18) * mm, "mid": v(35.32, -19.11) * mm, "end": v(35.5, -18.93) * mm});
            skArc(sketch, "E13.24.8", {"start": v(33.14, -19.07) * mm, "mid": v(34.1, -19.18) * mm, "end": v(35.07, -19.18) * mm});
            skArc(sketch, "E13.24.9", {"start": v(32.87, -18.98) * mm, "mid": v(33, -19.04) * mm, "end": v(33.14, -19.07) * mm});
            skLineSegment(sketch, "E13.24.10", {"start": v(32.87, -18.98) * mm, "end": v(31.85, -18.39) * mm});
            skArc(sketch, "E13.24.11", {"start": v(31.85, -18.39) * mm, "mid": v(31.25, -18.3) * mm, "end": v(30.76, -18.67) * mm});
            skArc(sketch, "E13.25.0", {"start": v(34.95, -8.55) * mm, "mid": v(35.04, -9.15) * mm, "end": v(35.52, -9.52) * mm});
            skLineSegment(sketch, "E13.25.1", {"start": v(36.66, -9.82) * mm, "end": v(35.52, -9.52) * mm});
            skArc(sketch, "E13.25.2", {"start": v(36.92, -9.95) * mm, "mid": v(36.8, -9.87) * mm, "end": v(36.66, -9.82) * mm});
            skArc(sketch, "E13.25.3", {"start": v(36.92, -9.95) * mm, "mid": v(37.68, -10.56) * mm, "end": v(38.37, -11.24) * mm});
            skArc(sketch, "E13.25.4", {"start": v(38.48, -11.71) * mm, "mid": v(38.49, -11.46) * mm, "end": v(38.37, -11.24) * mm});
            skLineSegment(sketch, "E13.25.5", {"start": v(38.48, -11.71) * mm, "end": v(38.38, -12.1) * mm});
            skLineSegment(sketch, "E13.25.6", {"start": v(38.24, -12.48) * mm, "end": v(38.38, -12.1) * mm});
            skArc(sketch, "E13.25.7", {"start": v(37.87, -12.8) * mm, "mid": v(38.1, -12.69) * mm, "end": v(38.24, -12.48) * mm});
            skArc(sketch, "E13.25.8", {"start": v(35.95, -13.03) * mm, "mid": v(36.92, -12.96) * mm, "end": v(37.87, -12.8) * mm});
            skArc(sketch, "E13.25.9", {"start": v(35.67, -12.98) * mm, "mid": v(35.8, -13.02) * mm, "end": v(35.95, -13.03) * mm});
            skLineSegment(sketch, "E13.25.10", {"start": v(35.67, -12.98) * mm, "end": v(34.56, -12.58) * mm});
            skArc(sketch, "E13.25.11", {"start": v(34.56, -12.58) * mm, "mid": v(33.95, -12.6) * mm, "end": v(33.54, -13.04) * mm});
            skArc(sketch, "E13.26.0", {"start": v(35.9, -2.36) * mm, "mid": v(36.1, -2.93) * mm, "end": v(36.63, -3.2) * mm});
            skLineSegment(sketch, "E13.26.1", {"start": v(37.81, -3.3) * mm, "end": v(36.63, -3.2) * mm});
            skArc(sketch, "E13.26.2", {"start": v(38.1, -3.39) * mm, "mid": v(37.95, -3.33) * mm, "end": v(37.81, -3.3) * mm});
            skArc(sketch, "E13.26.3", {"start": v(38.1, -3.39) * mm, "mid": v(38.94, -3.85) * mm, "end": v(39.74, -4.4) * mm});
            skArc(sketch, "E13.26.4", {"start": v(39.93, -4.85) * mm, "mid": v(39.9, -4.6) * mm, "end": v(39.74, -4.4) * mm});
            skLineSegment(sketch, "E13.26.5", {"start": v(39.93, -4.85) * mm, "end": v(39.9, -5.25) * mm});
            skLineSegment(sketch, "E13.26.6", {"start": v(39.83, -5.65) * mm, "end": v(39.9, -5.25) * mm});
            skArc(sketch, "E13.26.7", {"start": v(39.52, -6.03) * mm, "mid": v(39.72, -5.88) * mm, "end": v(39.83, -5.65) * mm});
            skArc(sketch, "E13.26.8", {"start": v(37.67, -6.59) * mm, "mid": v(38.6, -6.36) * mm, "end": v(39.52, -6.03) * mm});
            skArc(sketch, "E13.26.9", {"start": v(37.38, -6.6) * mm, "mid": v(37.52, -6.6) * mm, "end": v(37.67, -6.59) * mm});
            skLineSegment(sketch, "E13.26.10", {"start": v(37.38, -6.6) * mm, "end": v(36.22, -6.39) * mm});
            skArc(sketch, "E13.26.11", {"start": v(36.22, -6.39) * mm, "mid": v(35.63, -6.51) * mm, "end": v(35.3, -7.02) * mm});
            skArc(sketch, "E13.27.0", {"start": v(35.77, 3.92) * mm, "mid": v(36.06, 3.38) * mm, "end": v(36.63, 3.2) * mm});
            skLineSegment(sketch, "E13.27.1", {"start": v(37.81, 3.3) * mm, "end": v(36.63, 3.2) * mm});
            skArc(sketch, "E13.27.2", {"start": v(38.1, 3.28) * mm, "mid": v(37.96, 3.3) * mm, "end": v(37.81, 3.3) * mm});
            skArc(sketch, "E13.27.3", {"start": v(38.1, 3.28) * mm, "mid": v(39.02, 2.97) * mm, "end": v(39.9, 2.56) * mm});
            skArc(sketch, "E13.27.4", {"start": v(40.17, 2.16) * mm, "mid": v(40.08, 2.4) * mm, "end": v(39.9, 2.56) * mm});
            skLineSegment(sketch, "E13.27.5", {"start": v(40.17, 2.16) * mm, "end": v(40.2, 1.76) * mm});
            skLineSegment(sketch, "E13.27.6", {"start": v(40.2, 1.35) * mm, "end": v(40.2, 1.76) * mm});
            skArc(sketch, "E13.27.7", {"start": v(39.97, 0.92) * mm, "mid": v(40.14, 1.1) * mm, "end": v(40.2, 1.35) * mm});
            skArc(sketch, "E13.27.8", {"start": v(38.24, 0.05) * mm, "mid": v(39.13, 0.44) * mm, "end": v(39.97, 0.92) * mm});
            skArc(sketch, "E13.27.9", {"start": v(37.96, 0) * mm, "mid": v(38.1, 0.01) * mm, "end": v(38.24, 0.05) * mm});
            skLineSegment(sketch, "E13.27.10", {"start": v(37.96, 0) * mm, "end": v(36.77, 0) * mm});
            skArc(sketch, "E13.27.11", {"start": v(36.77, 0) * mm, "mid": v(36.22, -0.23) * mm, "end": v(35.97, -0.78) * mm});
            skArc(sketch, "E13.28.0", {"start": v(34.55, 10.07) * mm, "mid": v(34.92, 9.6) * mm, "end": v(35.52, 9.52) * mm});
            skLineSegment(sketch, "E13.28.1", {"start": v(36.66, 9.82) * mm, "end": v(35.52, 9.52) * mm});
            skArc(sketch, "E13.28.2", {"start": v(36.95, 9.85) * mm, "mid": v(36.8, 9.85) * mm, "end": v(36.66, 9.82) * mm});
            skArc(sketch, "E13.28.3", {"start": v(36.95, 9.85) * mm, "mid": v(37.9, 9.7) * mm, "end": v(38.84, 9.45) * mm});
            skArc(sketch, "E13.28.4", {"start": v(39.18, 9.1) * mm, "mid": v(39.06, 9.32) * mm, "end": v(38.84, 9.45) * mm});
            skLineSegment(sketch, "E13.28.5", {"start": v(39.18, 9.1) * mm, "end": v(39.29, 8.7) * mm});
            skLineSegment(sketch, "E13.28.6", {"start": v(39.36, 8.31) * mm, "end": v(39.29, 8.7) * mm});
            skArc(sketch, "E13.28.7", {"start": v(39.2, 7.85) * mm, "mid": v(39.34, 8.06) * mm, "end": v(39.36, 8.31) * mm});
            skArc(sketch, "E13.28.8", {"start": v(37.65, 6.7) * mm, "mid": v(38.46, 7.23) * mm, "end": v(39.2, 7.85) * mm});
            skArc(sketch, "E13.28.9", {"start": v(37.38, 6.6) * mm, "mid": v(37.52, 6.63) * mm, "end": v(37.65, 6.7) * mm});
            skLineSegment(sketch, "E13.28.10", {"start": v(37.38, 6.6) * mm, "end": v(36.22, 6.39) * mm});
            skArc(sketch, "E13.28.11", {"start": v(36.22, 6.39) * mm, "mid": v(35.7, 6.06) * mm, "end": v(35.56, 5.48) * mm});
            skArc(sketch, "E13.29.0", {"start": v(32.27, 15.91) * mm, "mid": v(32.73, 15.51) * mm, "end": v(33.33, 15.54) * mm});
            skLineSegment(sketch, "E13.29.1", {"start": v(34.4, 16.04) * mm, "end": v(33.33, 15.54) * mm});
            skArc(sketch, "E13.29.2", {"start": v(34.68, 16.11) * mm, "mid": v(34.54, 16.1) * mm, "end": v(34.4, 16.04) * mm});
            skArc(sketch, "E13.29.3", {"start": v(34.68, 16.11) * mm, "mid": v(35.65, 16.13) * mm, "end": v(36.61, 16.05) * mm});
            skArc(sketch, "E13.29.4", {"start": v(37, 15.77) * mm, "mid": v(36.85, 15.96) * mm, "end": v(36.61, 16.05) * mm});
            skLineSegment(sketch, "E13.29.5", {"start": v(37, 15.77) * mm, "end": v(37.18, 15.4) * mm});
            skLineSegment(sketch, "E13.29.6", {"start": v(37.32, 15.02) * mm, "end": v(37.18, 15.4) * mm});
            skArc(sketch, "E13.29.7", {"start": v(37.24, 14.54) * mm, "mid": v(37.34, 14.77) * mm, "end": v(37.32, 15.02) * mm});
            skArc(sketch, "E13.29.8", {"start": v(35.92, 13.13) * mm, "mid": v(36.62, 13.8) * mm, "end": v(37.24, 14.54) * mm});
            skArc(sketch, "E13.29.9", {"start": v(35.67, 12.98) * mm, "mid": v(35.8, 13.04) * mm, "end": v(35.92, 13.13) * mm});
            skLineSegment(sketch, "E13.29.10", {"start": v(35.67, 12.98) * mm, "end": v(34.56, 12.58) * mm});
            skArc(sketch, "E13.29.11", {"start": v(34.56, 12.58) * mm, "mid": v(34.1, 12.17) * mm, "end": v(34.07, 11.57) * mm});
            skArc(sketch, "E13.30.0", {"start": v(29.02, 21.28) * mm, "mid": v(29.53, 20.96) * mm, "end": v(30.12, 21.1) * mm});
            skLineSegment(sketch, "E13.30.1", {"start": v(31.1, 21.77) * mm, "end": v(30.12, 21.1) * mm});
            skArc(sketch, "E13.30.2", {"start": v(31.36, 21.9) * mm, "mid": v(31.22, 21.84) * mm, "end": v(31.1, 21.77) * mm});
            skArc(sketch, "E13.30.3", {"start": v(31.36, 21.9) * mm, "mid": v(32.3, 22.08) * mm, "end": v(33.27, 22.17) * mm});
            skArc(sketch, "E13.30.4", {"start": v(33.7, 21.95) * mm, "mid": v(33.52, 22.12) * mm, "end": v(33.27, 22.17) * mm});
            skLineSegment(sketch, "E13.30.5", {"start": v(33.7, 21.95) * mm, "end": v(33.94, 21.62) * mm});
            skLineSegment(sketch, "E13.30.6", {"start": v(34.14, 21.27) * mm, "end": v(33.94, 21.62) * mm});
            skArc(sketch, "E13.30.7", {"start": v(34.15, 20.78) * mm, "mid": v(34.2, 21.03) * mm, "end": v(34.14, 21.27) * mm});
            skArc(sketch, "E13.30.8", {"start": v(33.1, 19.17) * mm, "mid": v(33.66, 19.95) * mm, "end": v(34.15, 20.78) * mm});
            skArc(sketch, "E13.30.9", {"start": v(32.87, 18.98) * mm, "mid": v(32.99, 19.06) * mm, "end": v(33.1, 19.17) * mm});
            skLineSegment(sketch, "E13.30.10", {"start": v(32.87, 18.98) * mm, "end": v(31.85, 18.39) * mm});
            skArc(sketch, "E13.30.11", {"start": v(31.85, 18.39) * mm, "mid": v(31.48, 17.9) * mm, "end": v(31.55, 17.3) * mm});
            skArc(sketch, "E13.31.0", {"start": v(24.88, 26) * mm, "mid": v(25.45, 25.77) * mm, "end": v(26, 26) * mm});
            skLineSegment(sketch, "E13.31.1", {"start": v(26.84, 26.84) * mm, "end": v(26, 26) * mm});
            skArc(sketch, "E13.31.2", {"start": v(27.08, 27) * mm, "mid": v(26.95, 26.93) * mm, "end": v(26.84, 26.84) * mm});
            skArc(sketch, "E13.31.3", {"start": v(27.08, 27) * mm, "mid": v(27.98, 27.35) * mm, "end": v(28.91, 27.6) * mm});
            skArc(sketch, "E13.31.4", {"start": v(29.38, 27.47) * mm, "mid": v(29.17, 27.6) * mm, "end": v(28.91, 27.6) * mm});
            skLineSegment(sketch, "E13.31.5", {"start": v(29.38, 27.47) * mm, "end": v(29.67, 27.19) * mm});
            skLineSegment(sketch, "E13.31.6", {"start": v(29.93, 26.88) * mm, "end": v(29.67, 27.19) * mm});
            skArc(sketch, "E13.31.7", {"start": v(30.02, 26.4) * mm, "mid": v(30.04, 26.65) * mm, "end": v(29.93, 26.88) * mm});
            skArc(sketch, "E13.31.8", {"start": v(29.26, 24.62) * mm, "mid": v(29.69, 25.5) * mm, "end": v(30.02, 26.4) * mm});
            skArc(sketch, "E13.31.9", {"start": v(29.08, 24.4) * mm, "mid": v(29.18, 24.5) * mm, "end": v(29.26, 24.62) * mm});
            skLineSegment(sketch, "E13.31.10", {"start": v(29.08, 24.4) * mm, "end": v(28.17, 23.64) * mm});
            skArc(sketch, "E13.31.11", {"start": v(28.17, 23.64) * mm, "mid": v(27.89, 23.1) * mm, "end": v(28.06, 22.52) * mm});
            skArc(sketch, "E13.32.0", {"start": v(20, 29.92) * mm, "mid": v(20.59, 29.8) * mm, "end": v(21.1, 30.12) * mm});
            skLineSegment(sketch, "E13.32.1", {"start": v(21.77, 31.1) * mm, "end": v(21.1, 30.12) * mm});
            skArc(sketch, "E13.32.2", {"start": v(21.98, 31.3) * mm, "mid": v(21.86, 31.2) * mm, "end": v(21.77, 31.1) * mm});
            skArc(sketch, "E13.32.3", {"start": v(21.98, 31.3) * mm, "mid": v(22.8, 31.8) * mm, "end": v(23.68, 32.21) * mm});
            skArc(sketch, "E13.32.4", {"start": v(24.17, 32.16) * mm, "mid": v(23.93, 32.25) * mm, "end": v(23.68, 32.21) * mm});
            skLineSegment(sketch, "E13.32.5", {"start": v(24.17, 32.16) * mm, "end": v(24.5, 31.92) * mm});
            skLineSegment(sketch, "E13.32.6", {"start": v(24.8, 31.67) * mm, "end": v(24.5, 31.92) * mm});
            skArc(sketch, "E13.32.7", {"start": v(24.98, 31.21) * mm, "mid": v(24.95, 31.46) * mm, "end": v(24.8, 31.67) * mm});
            skArc(sketch, "E13.32.8", {"start": v(24.54, 29.33) * mm, "mid": v(24.8, 30.26) * mm, "end": v(24.98, 31.21) * mm});
            skArc(sketch, "E13.32.9", {"start": v(24.4, 29.08) * mm, "mid": v(24.48, 29.2) * mm, "end": v(24.54, 29.33) * mm});
            skLineSegment(sketch, "E13.32.10", {"start": v(24.4, 29.08) * mm, "end": v(23.64, 28.17) * mm});
            skArc(sketch, "E13.32.11", {"start": v(23.64, 28.17) * mm, "mid": v(23.45, 27.6) * mm, "end": v(23.72, 27.06) * mm});
            skArc(sketch, "E13.33.0", {"start": v(14.5, 32.94) * mm, "mid": v(15.1, 32.92) * mm, "end": v(15.54, 33.33) * mm});
            skLineSegment(sketch, "E13.33.1", {"start": v(16.04, 34.4) * mm, "end": v(15.54, 33.33) * mm});
            skArc(sketch, "E13.33.2", {"start": v(16.2, 34.64) * mm, "mid": v(16.11, 34.53) * mm, "end": v(16.04, 34.4) * mm});
            skArc(sketch, "E13.33.3", {"start": v(16.2, 34.64) * mm, "mid": v(16.94, 35.27) * mm, "end": v(17.73, 35.83) * mm});
            skArc(sketch, "E13.33.4", {"start": v(18.22, 35.86) * mm, "mid": v(17.97, 35.91) * mm, "end": v(17.73, 35.83) * mm});
            skLineSegment(sketch, "E13.33.5", {"start": v(18.22, 35.86) * mm, "end": v(18.58, 35.7) * mm});
            skLineSegment(sketch, "E13.33.6", {"start": v(18.93, 35.5) * mm, "end": v(18.58, 35.7) * mm});
            skArc(sketch, "E13.33.7", {"start": v(19.18, 35.07) * mm, "mid": v(19.11, 35.32) * mm, "end": v(18.93, 35.5) * mm});
            skArc(sketch, "E13.33.8", {"start": v(19.07, 33.14) * mm, "mid": v(19.18, 34.1) * mm, "end": v(19.18, 35.07) * mm});
            skArc(sketch, "E13.33.9", {"start": v(18.98, 32.87) * mm, "mid": v(19.04, 33) * mm, "end": v(19.07, 33.14) * mm});
            skLineSegment(sketch, "E13.33.10", {"start": v(18.98, 32.87) * mm, "end": v(18.39, 31.85) * mm});
            skArc(sketch, "E13.33.11", {"start": v(18.39, 31.85) * mm, "mid": v(18.3, 31.25) * mm, "end": v(18.67, 30.76) * mm});
            skArc(sketch, "E13.34.0", {"start": v(8.55, 34.95) * mm, "mid": v(9.15, 35.04) * mm, "end": v(9.52, 35.52) * mm});
            skLineSegment(sketch, "E13.34.1", {"start": v(9.82, 36.66) * mm, "end": v(9.52, 35.52) * mm});
            skArc(sketch, "E13.34.2", {"start": v(9.95, 36.92) * mm, "mid": v(9.87, 36.8) * mm, "end": v(9.82, 36.66) * mm});
            skArc(sketch, "E13.34.3", {"start": v(9.95, 36.92) * mm, "mid": v(10.56, 37.68) * mm, "end": v(11.24, 38.37) * mm});
            skArc(sketch, "E13.34.4", {"start": v(11.71, 38.48) * mm, "mid": v(11.46, 38.49) * mm, "end": v(11.24, 38.37) * mm});
            skLineSegment(sketch, "E13.34.5", {"start": v(11.71, 38.48) * mm, "end": v(12.1, 38.38) * mm});
            skLineSegment(sketch, "E13.34.6", {"start": v(12.48, 38.24) * mm, "end": v(12.1, 38.38) * mm});
            skArc(sketch, "E13.34.7", {"start": v(12.8, 37.87) * mm, "mid": v(12.69, 38.1) * mm, "end": v(12.48, 38.24) * mm});
            skArc(sketch, "E13.34.8", {"start": v(13.03, 35.95) * mm, "mid": v(12.96, 36.92) * mm, "end": v(12.8, 37.87) * mm});
            skArc(sketch, "E13.34.9", {"start": v(12.98, 35.67) * mm, "mid": v(13.02, 35.8) * mm, "end": v(13.03, 35.95) * mm});
            skLineSegment(sketch, "E13.34.10", {"start": v(12.98, 35.67) * mm, "end": v(12.58, 34.56) * mm});
            skArc(sketch, "E13.34.11", {"start": v(12.58, 34.56) * mm, "mid": v(12.6, 33.95) * mm, "end": v(13.04, 33.54) * mm});
            skArc(sketch, "E13.35.0", {"start": v(2.36, 35.9) * mm, "mid": v(2.93, 36.1) * mm, "end": v(3.2, 36.63) * mm});
            skLineSegment(sketch, "E13.35.1", {"start": v(3.3, 37.81) * mm, "end": v(3.2, 36.63) * mm});
            skArc(sketch, "E13.35.2", {"start": v(3.39, 38.1) * mm, "mid": v(3.33, 37.95) * mm, "end": v(3.3, 37.81) * mm});
            skArc(sketch, "E13.35.3", {"start": v(3.39, 38.1) * mm, "mid": v(3.85, 38.94) * mm, "end": v(4.4, 39.74) * mm});
            skArc(sketch, "E13.35.4", {"start": v(4.85, 39.93) * mm, "mid": v(4.6, 39.9) * mm, "end": v(4.4, 39.74) * mm});
            skLineSegment(sketch, "E13.35.5", {"start": v(4.85, 39.93) * mm, "end": v(5.25, 39.9) * mm});
            skLineSegment(sketch, "E13.35.6", {"start": v(5.65, 39.83) * mm, "end": v(5.25, 39.9) * mm});
            skArc(sketch, "E13.35.7", {"start": v(6.03, 39.52) * mm, "mid": v(5.88, 39.72) * mm, "end": v(5.65, 39.83) * mm});
            skArc(sketch, "E13.35.8", {"start": v(6.59, 37.67) * mm, "mid": v(6.36, 38.6) * mm, "end": v(6.03, 39.52) * mm});
            skArc(sketch, "E13.35.9", {"start": v(6.6, 37.38) * mm, "mid": v(6.6, 37.52) * mm, "end": v(6.59, 37.67) * mm});
            skLineSegment(sketch, "E13.35.10", {"start": v(6.6, 37.38) * mm, "end": v(6.39, 36.22) * mm});
            skArc(sketch, "E13.35.11", {"start": v(6.39, 36.22) * mm, "mid": v(6.51, 35.63) * mm, "end": v(7.02, 35.3) * mm});
            skArc(sketch, "E14.trimOffspring", {"start": v(2.36, 35.9) * mm, "mid": v(1.57, 35.95) * mm, "end": v(0.78, 35.97) * mm});
            skArc(sketch, "E15.trimOffspring", {"start": v(8.55, 34.95) * mm, "mid": v(7.79, 35.13) * mm, "end": v(7.02, 35.3) * mm});
            skArc(sketch, "E16.trimOffspring", {"start": v(14.5, 32.94) * mm, "mid": v(13.77, 33.24) * mm, "end": v(13.04, 33.54) * mm});
            skArc(sketch, "E17.trimOffspring", {"start": v(20, 29.92) * mm, "mid": v(19.33, 30.35) * mm, "end": v(18.67, 30.76) * mm});
            skArc(sketch, "E18.trimOffspring", {"start": v(-10.07, 34.55) * mm, "mid": v(-10.82, 34.32) * mm, "end": v(-11.57, 34.07) * mm});
            skArc(sketch, "E19.trimOffspring", {"start": v(24.88, 26) * mm, "mid": v(24.3, 26.53) * mm, "end": v(23.72, 27.06) * mm});
            skArc(sketch, "E20.trimOffspring", {"start": v(-15.91, 32.27) * mm, "mid": v(-16.62, 31.92) * mm, "end": v(-17.3, 31.55) * mm});
            skArc(sketch, "E21.trimOffspring", {"start": v(29.02, 21.28) * mm, "mid": v(28.55, 21.9) * mm, "end": v(28.06, 22.52) * mm});
            skArc(sketch, "E22.trimOffspring", {"start": v(32.27, 15.91) * mm, "mid": v(31.92, 16.62) * mm, "end": v(31.55, 17.3) * mm});
            skArc(sketch, "E23.trimOffspring", {"start": v(34.55, 10.07) * mm, "mid": v(34.32, 10.82) * mm, "end": v(34.07, 11.57) * mm});
            skArc(sketch, "E24.trimOffspring", {"start": v(35.77, 3.92) * mm, "mid": v(35.68, 4.7) * mm, "end": v(35.56, 5.48) * mm});
            skArc(sketch, "E25.trimOffspring", {"start": v(35.9, -2.36) * mm, "mid": v(35.95, -1.57) * mm, "end": v(35.97, -0.78) * mm});
            skArc(sketch, "E26.trimOffspring", {"start": v(34.95, -8.55) * mm, "mid": v(35.13, -7.79) * mm, "end": v(35.3, -7.02) * mm});
            skArc(sketch, "E27.trimOffspring", {"start": v(32.94, -14.5) * mm, "mid": v(33.24, -13.77) * mm, "end": v(33.54, -13.04) * mm});
            skArc(sketch, "E28.trimOffspring", {"start": v(29.92, -20) * mm, "mid": v(30.35, -19.33) * mm, "end": v(30.76, -18.67) * mm});
            skArc(sketch, "E29.trimOffspring", {"start": v(26, -24.88) * mm, "mid": v(26.53, -24.3) * mm, "end": v(27.06, -23.72) * mm});
            skArc(sketch, "E30.trimOffspring", {"start": v(21.28, -29.02) * mm, "mid": v(21.9, -28.55) * mm, "end": v(22.52, -28.06) * mm});
            skArc(sketch, "E31.trimOffspring", {"start": v(15.91, -32.27) * mm, "mid": v(16.62, -31.92) * mm, "end": v(17.3, -31.55) * mm});
            skArc(sketch, "E32.trimOffspring", {"start": v(10.07, -34.55) * mm, "mid": v(10.82, -34.32) * mm, "end": v(11.57, -34.07) * mm});
            skArc(sketch, "E33.trimOffspring", {"start": v(3.92, -35.77) * mm, "mid": v(4.7, -35.68) * mm, "end": v(5.48, -35.56) * mm});
            skArc(sketch, "E34.trimOffspring", {"start": v(-2.36, -35.9) * mm, "mid": v(-1.57, -35.95) * mm, "end": v(-0.78, -35.97) * mm});
            skArc(sketch, "E35.trimOffspring", {"start": v(-8.55, -34.95) * mm, "mid": v(-7.79, -35.13) * mm, "end": v(-7.02, -35.3) * mm});
            skArc(sketch, "E36.trimOffspring", {"start": v(-14.5, -32.94) * mm, "mid": v(-13.77, -33.24) * mm, "end": v(-13.04, -33.54) * mm});
            skArc(sketch, "E37.trimOffspring", {"start": v(-24.88, -26) * mm, "mid": v(-24.3, -26.53) * mm, "end": v(-23.72, -27.06) * mm});
            skArc(sketch, "E38.trimOffspring", {"start": v(-29.02, -21.28) * mm, "mid": v(-28.55, -21.9) * mm, "end": v(-28.06, -22.52) * mm});
            skArc(sketch, "E39.trimOffspring", {"start": v(-32.27, -15.91) * mm, "mid": v(-31.92, -16.62) * mm, "end": v(-31.55, -17.3) * mm});
            skArc(sketch, "E40.trimOffspring", {"start": v(-20, -29.92) * mm, "mid": v(-19.33, -30.35) * mm, "end": v(-18.67, -30.76) * mm});
            skArc(sketch, "E41.trimOffspring", {"start": v(-34.55, -10.07) * mm, "mid": v(-34.32, -10.82) * mm, "end": v(-34.07, -11.57) * mm});
            skArc(sketch, "E42.trimOffspring", {"start": v(-35.77, -3.92) * mm, "mid": v(-35.68, -4.7) * mm, "end": v(-35.56, -5.48) * mm});
            skArc(sketch, "E43.trimOffspring", {"start": v(-35.9, 2.36) * mm, "mid": v(-35.95, 1.57) * mm, "end": v(-35.97, 0.78) * mm});
            skArc(sketch, "E44.trimOffspring", {"start": v(-34.95, 8.55) * mm, "mid": v(-35.13, 7.79) * mm, "end": v(-35.3, 7.02) * mm});
            skArc(sketch, "E45.trimOffspring", {"start": v(-32.94, 14.5) * mm, "mid": v(-33.24, 13.77) * mm, "end": v(-33.54, 13.04) * mm});
            skArc(sketch, "E46.trimOffspring", {"start": v(-29.92, 20) * mm, "mid": v(-30.35, 19.33) * mm, "end": v(-30.76, 18.67) * mm});
            skArc(sketch, "E47.trimOffspring", {"start": v(-26, 24.88) * mm, "mid": v(-26.53, 24.3) * mm, "end": v(-27.06, 23.72) * mm});
            skArc(sketch, "E48.trimOffspring", {"start": v(-21.28, 29.02) * mm, "mid": v(-21.9, 28.55) * mm, "end": v(-22.52, 28.06) * mm});
            skSolve(sketch);
        }
        {
            var Q0;
            Q0 = qSketchRegion(id + "F0", true);
            extrude(context, id + "F1", {"entities" : qUnion([Q0]), "depth" : 6.35 * mm});
        }
        {
            var Q0;
            Q0=makeQuery(id+"F1.opExtrude","CAP_FACE",FACE,{"disambiguationData":[OSD([sQuery(id+"F0.wireOp",EDGE,"E0"),sQuery(id+"F0.wireOp",EDGE,"E1.trimOffspring"),sQuery(id+"F0.wireOp",EDGE,"E2"),sQuery(id+"F0.wireOp",EDGE,"E3"),sQuery(id+"F0.wireOp",EDGE,"E4.MirrorCS"),sQuery(id+"F0.wireOp",EDGE,"E5.MirrorCS"),sQuery(id+"F0.wireOp",EDGE,"E6.MirrorCS"),sQuery(id+"F0.wireOp",EDGE,"E7.filletArc"),sQuery(id+"F0.wireOp",EDGE,"E8.filletArc"),sQuery(id+"F0.wireOp",EDGE,"E9.filletArc"),sQuery(id+"F0.wireOp",EDGE,"E10.filletArc"),sQuery(id+"F0.wireOp",EDGE,"E11.filletArc"),sQuery(id+"F0.wireOp",EDGE,"E12.filletArc"),sQuery(id+"F0.wireOp",EDGE,"E13.1.0"),sQuery(id+"F0.wireOp",EDGE,"E13.1.1"),sQuery(id+"F0.wireOp",EDGE,"E13.1.2"),sQuery(id+"F0.wireOp",EDGE,"E13.1.3"),sQuery(id+"F0.wireOp",EDGE,"E13.1.4"),sQuery(id+"F0.wireOp",EDGE,"E13.1.5"),sQuery(id+"F0.wireOp",EDGE,"E13.1.6"),sQuery(id+"F0.wireOp",EDGE,"E13.1.7"),sQuery(id+"F0.wireOp",EDGE,"E13.1.8"),sQuery(id+"F0.wireOp",EDGE,"E13.1.9"),sQuery(id+"F0.wireOp",EDGE,"E13.1.10"),sQuery(id+"F0.wireOp",EDGE,"E13.1.11"),sQuery(id+"F0.wireOp",EDGE,"E13.2.0"),sQuery(id+"F0.wireOp",EDGE,"E13.2.1"),sQuery(id+"F0.wireOp",EDGE,"E13.2.2"),sQuery(id+"F0.wireOp",EDGE,"E13.2.3"),sQuery(id+"F0.wireOp",EDGE,"E13.2.4"),sQuery(id+"F0.wireOp",EDGE,"E13.2.5"),sQuery(id+"F0.wireOp",EDGE,"E13.2.6"),sQuery(id+"F0.wireOp",EDGE,"E13.2.7"),sQuery(id+"F0.wireOp",EDGE,"E13.2.8"),sQuery(id+"F0.wireOp",EDGE,"E13.2.9"),sQuery(id+"F0.wireOp",EDGE,"E13.2.10"),sQuery(id+"F0.wireOp",EDGE,"E13.2.11"),sQuery(id+"F0.wireOp",EDGE,"E13.3.0"),sQuery(id+"F0.wireOp",EDGE,"E13.3.1"),sQuery(id+"F0.wireOp",EDGE,"E13.3.2"),sQuery(id+"F0.wireOp",EDGE,"E13.3.3"),sQuery(id+"F0.wireOp",EDGE,"E13.3.4"),sQuery(id+"F0.wireOp",EDGE,"E13.3.5"),sQuery(id+"F0.wireOp",EDGE,"E13.3.6"),sQuery(id+"F0.wireOp",EDGE,"E13.3.7"),sQuery(id+"F0.wireOp",EDGE,"E13.3.8"),sQuery(id+"F0.wireOp",EDGE,"E13.3.9"),sQuery(id+"F0.wireOp",EDGE,"E13.3.10"),sQuery(id+"F0.wireOp",EDGE,"E13.3.11"),sQuery(id+"F0.wireOp",EDGE,"E13.4.0"),sQuery(id+"F0.wireOp",EDGE,"E13.4.1"),sQuery(id+"F0.wireOp",EDGE,"E13.4.2"),sQuery(id+"F0.wireOp",EDGE,"E13.4.3"),sQuery(id+"F0.wireOp",EDGE,"E13.4.4"),sQuery(id+"F0.wireOp",EDGE,"E13.4.5"),sQuery(id+"F0.wireOp",EDGE,"E13.4.6"),sQuery(id+"F0.wireOp",EDGE,"E13.4.7"),sQuery(id+"F0.wireOp",EDGE,"E13.4.8"),sQuery(id+"F0.wireOp",EDGE,"E13.4.9"),sQuery(id+"F0.wireOp",EDGE,"E13.4.10"),sQuery(id+"F0.wireOp",EDGE,"E13.4.11"),sQuery(id+"F0.wireOp",EDGE,"E13.5.0"),sQuery(id+"F0.wireOp",EDGE,"E13.5.1"),sQuery(id+"F0.wireOp",EDGE,"E13.5.2"),sQuery(id+"F0.wireOp",EDGE,"E13.5.3"),sQuery(id+"F0.wireOp",EDGE,"E13.5.4"),sQuery(id+"F0.wireOp",EDGE,"E13.5.5"),sQuery(id+"F0.wireOp",EDGE,"E13.5.6"),sQuery(id+"F0.wireOp",EDGE,"E13.5.7"),sQuery(id+"F0.wireOp",EDGE,"E13.5.8"),sQuery(id+"F0.wireOp",EDGE,"E13.5.9"),sQuery(id+"F0.wireOp",EDGE,"E13.5.10"),sQuery(id+"F0.wireOp",EDGE,"E13.5.11"),sQuery(id+"F0.wireOp",EDGE,"E13.6.0"),sQuery(id+"F0.wireOp",EDGE,"E13.6.1"),sQuery(id+"F0.wireOp",EDGE,"E13.6.2"),sQuery(id+"F0.wireOp",EDGE,"E13.6.3"),sQuery(id+"F0.wireOp",EDGE,"E13.6.4"),sQuery(id+"F0.wireOp",EDGE,"E13.6.5"),sQuery(id+"F0.wireOp",EDGE,"E13.6.6"),sQuery(id+"F0.wireOp",EDGE,"E13.6.7"),sQuery(id+"F0.wireOp",EDGE,"E13.6.8"),sQuery(id+"F0.wireOp",EDGE,"E13.6.9"),sQuery(id+"F0.wireOp",EDGE,"E13.6.10"),sQuery(id+"F0.wireOp",EDGE,"E13.6.11"),sQuery(id+"F0.wireOp",EDGE,"E13.7.0"),sQuery(id+"F0.wireOp",EDGE,"E13.7.1"),sQuery(id+"F0.wireOp",EDGE,"E13.7.2"),sQuery(id+"F0.wireOp",EDGE,"E13.7.3"),sQuery(id+"F0.wireOp",EDGE,"E13.7.4"),sQuery(id+"F0.wireOp",EDGE,"E13.7.5"),sQuery(id+"F0.wireOp",EDGE,"E13.7.6"),sQuery(id+"F0.wireOp",EDGE,"E13.7.7"),sQuery(id+"F0.wireOp",EDGE,"E13.7.8"),sQuery(id+"F0.wireOp",EDGE,"E13.7.9"),sQuery(id+"F0.wireOp",EDGE,"E13.7.10"),sQuery(id+"F0.wireOp",EDGE,"E13.7.11"),sQuery(id+"F0.wireOp",EDGE,"E13.8.0"),sQuery(id+"F0.wireOp",EDGE,"E13.8.1"),sQuery(id+"F0.wireOp",EDGE,"E13.8.2"),sQuery(id+"F0.wireOp",EDGE,"E13.8.3"),sQuery(id+"F0.wireOp",EDGE,"E13.8.4"),sQuery(id+"F0.wireOp",EDGE,"E13.8.5"),sQuery(id+"F0.wireOp",EDGE,"E13.8.6"),sQuery(id+"F0.wireOp",EDGE,"E13.8.7"),sQuery(id+"F0.wireOp",EDGE,"E13.8.8"),sQuery(id+"F0.wireOp",EDGE,"E13.8.9"),sQuery(id+"F0.wireOp",EDGE,"E13.8.10"),sQuery(id+"F0.wireOp",EDGE,"E13.8.11"),sQuery(id+"F0.wireOp",EDGE,"E13.9.0"),sQuery(id+"F0.wireOp",EDGE,"E13.9.1"),sQuery(id+"F0.wireOp",EDGE,"E13.9.2"),sQuery(id+"F0.wireOp",EDGE,"E13.9.3"),sQuery(id+"F0.wireOp",EDGE,"E13.9.4"),sQuery(id+"F0.wireOp",EDGE,"E13.9.5"),sQuery(id+"F0.wireOp",EDGE,"E13.9.6"),sQuery(id+"F0.wireOp",EDGE,"E13.9.7"),sQuery(id+"F0.wireOp",EDGE,"E13.9.8"),sQuery(id+"F0.wireOp",EDGE,"E13.9.9"),sQuery(id+"F0.wireOp",EDGE,"E13.9.10"),sQuery(id+"F0.wireOp",EDGE,"E13.9.11"),sQuery(id+"F0.wireOp",EDGE,"E13.10.0"),sQuery(id+"F0.wireOp",EDGE,"E13.10.1"),sQuery(id+"F0.wireOp",EDGE,"E13.10.2"),sQuery(id+"F0.wireOp",EDGE,"E13.10.3"),sQuery(id+"F0.wireOp",EDGE,"E13.10.4"),sQuery(id+"F0.wireOp",EDGE,"E13.10.5"),sQuery(id+"F0.wireOp",EDGE,"E13.10.6"),sQuery(id+"F0.wireOp",EDGE,"E13.10.7"),sQuery(id+"F0.wireOp",EDGE,"E13.10.8"),sQuery(id+"F0.wireOp",EDGE,"E13.10.9"),sQuery(id+"F0.wireOp",EDGE,"E13.10.10"),sQuery(id+"F0.wireOp",EDGE,"E13.10.11"),sQuery(id+"F0.wireOp",EDGE,"E13.11.0"),sQuery(id+"F0.wireOp",EDGE,"E13.11.1"),sQuery(id+"F0.wireOp",EDGE,"E13.11.2"),sQuery(id+"F0.wireOp",EDGE,"E13.11.3"),sQuery(id+"F0.wireOp",EDGE,"E13.11.4"),sQuery(id+"F0.wireOp",EDGE,"E13.11.5"),sQuery(id+"F0.wireOp",EDGE,"E13.11.6"),sQuery(id+"F0.wireOp",EDGE,"E13.11.7"),sQuery(id+"F0.wireOp",EDGE,"E13.11.8"),sQuery(id+"F0.wireOp",EDGE,"E13.11.9"),sQuery(id+"F0.wireOp",EDGE,"E13.11.10"),sQuery(id+"F0.wireOp",EDGE,"E13.11.11"),sQuery(id+"F0.wireOp",EDGE,"E13.12.0"),sQuery(id+"F0.wireOp",EDGE,"E13.12.1"),sQuery(id+"F0.wireOp",EDGE,"E13.12.2"),sQuery(id+"F0.wireOp",EDGE,"E13.12.3"),sQuery(id+"F0.wireOp",EDGE,"E13.12.4"),sQuery(id+"F0.wireOp",EDGE,"E13.12.5"),sQuery(id+"F0.wireOp",EDGE,"E13.12.6"),sQuery(id+"F0.wireOp",EDGE,"E13.12.7"),sQuery(id+"F0.wireOp",EDGE,"E13.12.8"),sQuery(id+"F0.wireOp",EDGE,"E13.12.9"),sQuery(id+"F0.wireOp",EDGE,"E13.12.10"),sQuery(id+"F0.wireOp",EDGE,"E13.12.11"),sQuery(id+"F0.wireOp",EDGE,"E13.13.0"),sQuery(id+"F0.wireOp",EDGE,"E13.13.1"),sQuery(id+"F0.wireOp",EDGE,"E13.13.2"),sQuery(id+"F0.wireOp",EDGE,"E13.13.3"),sQuery(id+"F0.wireOp",EDGE,"E13.13.4"),sQuery(id+"F0.wireOp",EDGE,"E13.13.5"),sQuery(id+"F0.wireOp",EDGE,"E13.13.6"),sQuery(id+"F0.wireOp",EDGE,"E13.13.7"),sQuery(id+"F0.wireOp",EDGE,"E13.13.8"),sQuery(id+"F0.wireOp",EDGE,"E13.13.9"),sQuery(id+"F0.wireOp",EDGE,"E13.13.10"),sQuery(id+"F0.wireOp",EDGE,"E13.13.11"),sQuery(id+"F0.wireOp",EDGE,"E13.14.0"),sQuery(id+"F0.wireOp",EDGE,"E13.14.1"),sQuery(id+"F0.wireOp",EDGE,"E13.14.2"),sQuery(id+"F0.wireOp",EDGE,"E13.14.3"),sQuery(id+"F0.wireOp",EDGE,"E13.14.4"),sQuery(id+"F0.wireOp",EDGE,"E13.14.5"),sQuery(id+"F0.wireOp",EDGE,"E13.14.6"),sQuery(id+"F0.wireOp",EDGE,"E13.14.7"),sQuery(id+"F0.wireOp",EDGE,"E13.14.8"),sQuery(id+"F0.wireOp",EDGE,"E13.14.9"),sQuery(id+"F0.wireOp",EDGE,"E13.14.10"),sQuery(id+"F0.wireOp",EDGE,"E13.14.11"),sQuery(id+"F0.wireOp",EDGE,"E13.15.0"),sQuery(id+"F0.wireOp",EDGE,"E13.15.1"),sQuery(id+"F0.wireOp",EDGE,"E13.15.2"),sQuery(id+"F0.wireOp",EDGE,"E13.15.3"),sQuery(id+"F0.wireOp",EDGE,"E13.15.4"),sQuery(id+"F0.wireOp",EDGE,"E13.15.5"),sQuery(id+"F0.wireOp",EDGE,"E13.15.6"),sQuery(id+"F0.wireOp",EDGE,"E13.15.7"),sQuery(id+"F0.wireOp",EDGE,"E13.15.8"),sQuery(id+"F0.wireOp",EDGE,"E13.15.9"),sQuery(id+"F0.wireOp",EDGE,"E13.15.10"),sQuery(id+"F0.wireOp",EDGE,"E13.15.11"),sQuery(id+"F0.wireOp",EDGE,"E13.16.0"),sQuery(id+"F0.wireOp",EDGE,"E13.16.1"),sQuery(id+"F0.wireOp",EDGE,"E13.16.2"),sQuery(id+"F0.wireOp",EDGE,"E13.16.3"),sQuery(id+"F0.wireOp",EDGE,"E13.16.4"),sQuery(id+"F0.wireOp",EDGE,"E13.16.5"),sQuery(id+"F0.wireOp",EDGE,"E13.16.6"),sQuery(id+"F0.wireOp",EDGE,"E13.16.7"),sQuery(id+"F0.wireOp",EDGE,"E13.16.8"),sQuery(id+"F0.wireOp",EDGE,"E13.16.9"),sQuery(id+"F0.wireOp",EDGE,"E13.16.10"),sQuery(id+"F0.wireOp",EDGE,"E13.16.11"),sQuery(id+"F0.wireOp",EDGE,"E13.17.0"),sQuery(id+"F0.wireOp",EDGE,"E13.17.1"),sQuery(id+"F0.wireOp",EDGE,"E13.17.2"),sQuery(id+"F0.wireOp",EDGE,"E13.17.3"),sQuery(id+"F0.wireOp",EDGE,"E13.17.4"),sQuery(id+"F0.wireOp",EDGE,"E13.17.5"),sQuery(id+"F0.wireOp",EDGE,"E13.17.6"),sQuery(id+"F0.wireOp",EDGE,"E13.17.7"),sQuery(id+"F0.wireOp",EDGE,"E13.17.8"),sQuery(id+"F0.wireOp",EDGE,"E13.17.9"),sQuery(id+"F0.wireOp",EDGE,"E13.17.10"),sQuery(id+"F0.wireOp",EDGE,"E13.17.11"),sQuery(id+"F0.wireOp",EDGE,"E13.18.0"),sQuery(id+"F0.wireOp",EDGE,"E13.18.1"),sQuery(id+"F0.wireOp",EDGE,"E13.18.2"),sQuery(id+"F0.wireOp",EDGE,"E13.18.3"),sQuery(id+"F0.wireOp",EDGE,"E13.18.4"),sQuery(id+"F0.wireOp",EDGE,"E13.18.5"),sQuery(id+"F0.wireOp",EDGE,"E13.18.6"),sQuery(id+"F0.wireOp",EDGE,"E13.18.7"),sQuery(id+"F0.wireOp",EDGE,"E13.18.8"),sQuery(id+"F0.wireOp",EDGE,"E13.18.9"),sQuery(id+"F0.wireOp",EDGE,"E13.18.10"),sQuery(id+"F0.wireOp",EDGE,"E13.18.11"),sQuery(id+"F0.wireOp",EDGE,"E13.19.0"),sQuery(id+"F0.wireOp",EDGE,"E13.19.1"),sQuery(id+"F0.wireOp",EDGE,"E13.19.2"),sQuery(id+"F0.wireOp",EDGE,"E13.19.3"),sQuery(id+"F0.wireOp",EDGE,"E13.19.4"),sQuery(id+"F0.wireOp",EDGE,"E13.19.5"),sQuery(id+"F0.wireOp",EDGE,"E13.19.6"),sQuery(id+"F0.wireOp",EDGE,"E13.19.7"),sQuery(id+"F0.wireOp",EDGE,"E13.19.8"),sQuery(id+"F0.wireOp",EDGE,"E13.19.9"),sQuery(id+"F0.wireOp",EDGE,"E13.19.10"),sQuery(id+"F0.wireOp",EDGE,"E13.19.11"),sQuery(id+"F0.wireOp",EDGE,"E13.20.0"),sQuery(id+"F0.wireOp",EDGE,"E13.20.1"),sQuery(id+"F0.wireOp",EDGE,"E13.20.2"),sQuery(id+"F0.wireOp",EDGE,"E13.20.3"),sQuery(id+"F0.wireOp",EDGE,"E13.20.4"),sQuery(id+"F0.wireOp",EDGE,"E13.20.5"),sQuery(id+"F0.wireOp",EDGE,"E13.20.6"),sQuery(id+"F0.wireOp",EDGE,"E13.20.7"),sQuery(id+"F0.wireOp",EDGE,"E13.20.8"),sQuery(id+"F0.wireOp",EDGE,"E13.20.9"),sQuery(id+"F0.wireOp",EDGE,"E13.20.10"),sQuery(id+"F0.wireOp",EDGE,"E13.20.11"),sQuery(id+"F0.wireOp",EDGE,"E13.21.0"),sQuery(id+"F0.wireOp",EDGE,"E13.21.1"),sQuery(id+"F0.wireOp",EDGE,"E13.21.2"),sQuery(id+"F0.wireOp",EDGE,"E13.21.3"),sQuery(id+"F0.wireOp",EDGE,"E13.21.4"),sQuery(id+"F0.wireOp",EDGE,"E13.21.5"),sQuery(id+"F0.wireOp",EDGE,"E13.21.6"),sQuery(id+"F0.wireOp",EDGE,"E13.21.7"),sQuery(id+"F0.wireOp",EDGE,"E13.21.8"),sQuery(id+"F0.wireOp",EDGE,"E13.21.9"),sQuery(id+"F0.wireOp",EDGE,"E13.21.10"),sQuery(id+"F0.wireOp",EDGE,"E13.21.11"),sQuery(id+"F0.wireOp",EDGE,"E13.22.0"),sQuery(id+"F0.wireOp",EDGE,"E13.22.1"),sQuery(id+"F0.wireOp",EDGE,"E13.22.2"),sQuery(id+"F0.wireOp",EDGE,"E13.22.3"),sQuery(id+"F0.wireOp",EDGE,"E13.22.4"),sQuery(id+"F0.wireOp",EDGE,"E13.22.5"),sQuery(id+"F0.wireOp",EDGE,"E13.22.6"),sQuery(id+"F0.wireOp",EDGE,"E13.22.7"),sQuery(id+"F0.wireOp",EDGE,"E13.22.8"),sQuery(id+"F0.wireOp",EDGE,"E13.22.9"),sQuery(id+"F0.wireOp",EDGE,"E13.22.10"),sQuery(id+"F0.wireOp",EDGE,"E13.22.11"),sQuery(id+"F0.wireOp",EDGE,"E13.23.0"),sQuery(id+"F0.wireOp",EDGE,"E13.23.1"),sQuery(id+"F0.wireOp",EDGE,"E13.23.2"),sQuery(id+"F0.wireOp",EDGE,"E13.23.3"),sQuery(id+"F0.wireOp",EDGE,"E13.23.4"),sQuery(id+"F0.wireOp",EDGE,"E13.23.5"),sQuery(id+"F0.wireOp",EDGE,"E13.23.6"),sQuery(id+"F0.wireOp",EDGE,"E13.23.7"),sQuery(id+"F0.wireOp",EDGE,"E13.23.8"),sQuery(id+"F0.wireOp",EDGE,"E13.23.9"),sQuery(id+"F0.wireOp",EDGE,"E13.23.10"),sQuery(id+"F0.wireOp",EDGE,"E13.23.11"),sQuery(id+"F0.wireOp",EDGE,"E13.24.0"),sQuery(id+"F0.wireOp",EDGE,"E13.24.1"),sQuery(id+"F0.wireOp",EDGE,"E13.24.2"),sQuery(id+"F0.wireOp",EDGE,"E13.24.3"),sQuery(id+"F0.wireOp",EDGE,"E13.24.4"),sQuery(id+"F0.wireOp",EDGE,"E13.24.5"),sQuery(id+"F0.wireOp",EDGE,"E13.24.6"),sQuery(id+"F0.wireOp",EDGE,"E13.24.7"),sQuery(id+"F0.wireOp",EDGE,"E13.24.8"),sQuery(id+"F0.wireOp",EDGE,"E13.24.9"),sQuery(id+"F0.wireOp",EDGE,"E13.24.10"),sQuery(id+"F0.wireOp",EDGE,"E13.24.11"),sQuery(id+"F0.wireOp",EDGE,"E13.25.0"),sQuery(id+"F0.wireOp",EDGE,"E13.25.1"),sQuery(id+"F0.wireOp",EDGE,"E13.25.2"),sQuery(id+"F0.wireOp",EDGE,"E13.25.3"),sQuery(id+"F0.wireOp",EDGE,"E13.25.4"),sQuery(id+"F0.wireOp",EDGE,"E13.25.5"),sQuery(id+"F0.wireOp",EDGE,"E13.25.6"),sQuery(id+"F0.wireOp",EDGE,"E13.25.7"),sQuery(id+"F0.wireOp",EDGE,"E13.25.8"),sQuery(id+"F0.wireOp",EDGE,"E13.25.9"),sQuery(id+"F0.wireOp",EDGE,"E13.25.10"),sQuery(id+"F0.wireOp",EDGE,"E13.25.11"),sQuery(id+"F0.wireOp",EDGE,"E13.26.0"),sQuery(id+"F0.wireOp",EDGE,"E13.26.1"),sQuery(id+"F0.wireOp",EDGE,"E13.26.2"),sQuery(id+"F0.wireOp",EDGE,"E13.26.3"),sQuery(id+"F0.wireOp",EDGE,"E13.26.4"),sQuery(id+"F0.wireOp",EDGE,"E13.26.5"),sQuery(id+"F0.wireOp",EDGE,"E13.26.6"),sQuery(id+"F0.wireOp",EDGE,"E13.26.7"),sQuery(id+"F0.wireOp",EDGE,"E13.26.8"),sQuery(id+"F0.wireOp",EDGE,"E13.26.9"),sQuery(id+"F0.wireOp",EDGE,"E13.26.10"),sQuery(id+"F0.wireOp",EDGE,"E13.26.11"),sQuery(id+"F0.wireOp",EDGE,"E13.27.0"),sQuery(id+"F0.wireOp",EDGE,"E13.27.1"),sQuery(id+"F0.wireOp",EDGE,"E13.27.2"),sQuery(id+"F0.wireOp",EDGE,"E13.27.3"),sQuery(id+"F0.wireOp",EDGE,"E13.27.4"),sQuery(id+"F0.wireOp",EDGE,"E13.27.5"),sQuery(id+"F0.wireOp",EDGE,"E13.27.6"),sQuery(id+"F0.wireOp",EDGE,"E13.27.7"),sQuery(id+"F0.wireOp",EDGE,"E13.27.8"),sQuery(id+"F0.wireOp",EDGE,"E13.27.9"),sQuery(id+"F0.wireOp",EDGE,"E13.27.10"),sQuery(id+"F0.wireOp",EDGE,"E13.27.11"),sQuery(id+"F0.wireOp",EDGE,"E13.28.0"),sQuery(id+"F0.wireOp",EDGE,"E13.28.1"),sQuery(id+"F0.wireOp",EDGE,"E13.28.2"),sQuery(id+"F0.wireOp",EDGE,"E13.28.3"),sQuery(id+"F0.wireOp",EDGE,"E13.28.4"),sQuery(id+"F0.wireOp",EDGE,"E13.28.5"),sQuery(id+"F0.wireOp",EDGE,"E13.28.6"),sQuery(id+"F0.wireOp",EDGE,"E13.28.7"),sQuery(id+"F0.wireOp",EDGE,"E13.28.8"),sQuery(id+"F0.wireOp",EDGE,"E13.28.9"),sQuery(id+"F0.wireOp",EDGE,"E13.28.10"),sQuery(id+"F0.wireOp",EDGE,"E13.28.11"),sQuery(id+"F0.wireOp",EDGE,"E13.29.0"),sQuery(id+"F0.wireOp",EDGE,"E13.29.1"),sQuery(id+"F0.wireOp",EDGE,"E13.29.2"),sQuery(id+"F0.wireOp",EDGE,"E13.29.3"),sQuery(id+"F0.wireOp",EDGE,"E13.29.4"),sQuery(id+"F0.wireOp",EDGE,"E13.29.5"),sQuery(id+"F0.wireOp",EDGE,"E13.29.6"),sQuery(id+"F0.wireOp",EDGE,"E13.29.7"),sQuery(id+"F0.wireOp",EDGE,"E13.29.8"),sQuery(id+"F0.wireOp",EDGE,"E13.29.9"),sQuery(id+"F0.wireOp",EDGE,"E13.29.10"),sQuery(id+"F0.wireOp",EDGE,"E13.29.11"),sQuery(id+"F0.wireOp",EDGE,"E13.30.0"),sQuery(id+"F0.wireOp",EDGE,"E13.30.1"),sQuery(id+"F0.wireOp",EDGE,"E13.30.2"),sQuery(id+"F0.wireOp",EDGE,"E13.30.3"),sQuery(id+"F0.wireOp",EDGE,"E13.30.4"),sQuery(id+"F0.wireOp",EDGE,"E13.30.5"),sQuery(id+"F0.wireOp",EDGE,"E13.30.6"),sQuery(id+"F0.wireOp",EDGE,"E13.30.7"),sQuery(id+"F0.wireOp",EDGE,"E13.30.8"),sQuery(id+"F0.wireOp",EDGE,"E13.30.9"),sQuery(id+"F0.wireOp",EDGE,"E13.30.10"),sQuery(id+"F0.wireOp",EDGE,"E13.30.11"),sQuery(id+"F0.wireOp",EDGE,"E13.31.0"),sQuery(id+"F0.wireOp",EDGE,"E13.31.1"),sQuery(id+"F0.wireOp",EDGE,"E13.31.2"),sQuery(id+"F0.wireOp",EDGE,"E13.31.3"),sQuery(id+"F0.wireOp",EDGE,"E13.31.4"),sQuery(id+"F0.wireOp",EDGE,"E13.31.5"),sQuery(id+"F0.wireOp",EDGE,"E13.31.6"),sQuery(id+"F0.wireOp",EDGE,"E13.31.7"),sQuery(id+"F0.wireOp",EDGE,"E13.31.8"),sQuery(id+"F0.wireOp",EDGE,"E13.31.9"),sQuery(id+"F0.wireOp",EDGE,"E13.31.10"),sQuery(id+"F0.wireOp",EDGE,"E13.31.11"),sQuery(id+"F0.wireOp",EDGE,"E13.32.0"),sQuery(id+"F0.wireOp",EDGE,"E13.32.1"),sQuery(id+"F0.wireOp",EDGE,"E13.32.2"),sQuery(id+"F0.wireOp",EDGE,"E13.32.3"),sQuery(id+"F0.wireOp",EDGE,"E13.32.4"),sQuery(id+"F0.wireOp",EDGE,"E13.32.5"),sQuery(id+"F0.wireOp",EDGE,"E13.32.6"),sQuery(id+"F0.wireOp",EDGE,"E13.32.7"),sQuery(id+"F0.wireOp",EDGE,"E13.32.8"),sQuery(id+"F0.wireOp",EDGE,"E13.32.9"),sQuery(id+"F0.wireOp",EDGE,"E13.32.10"),sQuery(id+"F0.wireOp",EDGE,"E13.32.11"),sQuery(id+"F0.wireOp",EDGE,"E13.33.0"),sQuery(id+"F0.wireOp",EDGE,"E13.33.1"),sQuery(id+"F0.wireOp",EDGE,"E13.33.2"),sQuery(id+"F0.wireOp",EDGE,"E13.33.3"),sQuery(id+"F0.wireOp",EDGE,"E13.33.4"),sQuery(id+"F0.wireOp",EDGE,"E13.33.5"),sQuery(id+"F0.wireOp",EDGE,"E13.33.6"),sQuery(id+"F0.wireOp",EDGE,"E13.33.7"),sQuery(id+"F0.wireOp",EDGE,"E13.33.8"),sQuery(id+"F0.wireOp",EDGE,"E13.33.9"),sQuery(id+"F0.wireOp",EDGE,"E13.33.10"),sQuery(id+"F0.wireOp",EDGE,"E13.33.11"),sQuery(id+"F0.wireOp",EDGE,"E13.34.0"),sQuery(id+"F0.wireOp",EDGE,"E13.34.1"),sQuery(id+"F0.wireOp",EDGE,"E13.34.2"),sQuery(id+"F0.wireOp",EDGE,"E13.34.3"),sQuery(id+"F0.wireOp",EDGE,"E13.34.4"),sQuery(id+"F0.wireOp",EDGE,"E13.34.5"),sQuery(id+"F0.wireOp",EDGE,"E13.34.6"),sQuery(id+"F0.wireOp",EDGE,"E13.34.7"),sQuery(id+"F0.wireOp",EDGE,"E13.34.8"),sQuery(id+"F0.wireOp",EDGE,"E13.34.9"),sQuery(id+"F0.wireOp",EDGE,"E13.34.10"),sQuery(id+"F0.wireOp",EDGE,"E13.34.11"),sQuery(id+"F0.wireOp",EDGE,"E13.35.0"),sQuery(id+"F0.wireOp",EDGE,"E13.35.1"),sQuery(id+"F0.wireOp",EDGE,"E13.35.2"),sQuery(id+"F0.wireOp",EDGE,"E13.35.3"),sQuery(id+"F0.wireOp",EDGE,"E13.35.4"),sQuery(id+"F0.wireOp",EDGE,"E13.35.5"),sQuery(id+"F0.wireOp",EDGE,"E13.35.6"),sQuery(id+"F0.wireOp",EDGE,"E13.35.7"),sQuery(id+"F0.wireOp",EDGE,"E13.35.8"),sQuery(id+"F0.wireOp",EDGE,"E13.35.9"),sQuery(id+"F0.wireOp",EDGE,"E13.35.10"),sQuery(id+"F0.wireOp",EDGE,"E13.35.11"),sQuery(id+"F0.wireOp",EDGE,"E14.trimOffspring"),sQuery(id+"F0.wireOp",EDGE,"E15.trimOffspring"),sQuery(id+"F0.wireOp",EDGE,"E16.trimOffspring"),sQuery(id+"F0.wireOp",EDGE,"E17.trimOffspring"),sQuery(id+"F0.wireOp",EDGE,"E18.trimOffspring"),sQuery(id+"F0.wireOp",EDGE,"E19.trimOffspring"),sQuery(id+"F0.wireOp",EDGE,"E20.trimOffspring"),sQuery(id+"F0.wireOp",EDGE,"E21.trimOffspring"),sQuery(id+"F0.wireOp",EDGE,"E22.trimOffspring"),sQuery(id+"F0.wireOp",EDGE,"E23.trimOffspring"),sQuery(id+"F0.wireOp",EDGE,"E24.trimOffspring"),sQuery(id+"F0.wireOp",EDGE,"E25.trimOffspring"),sQuery(id+"F0.wireOp",EDGE,"E26.trimOffspring"),sQuery(id+"F0.wireOp",EDGE,"E27.trimOffspring"),sQuery(id+"F0.wireOp",EDGE,"E28.trimOffspring"),sQuery(id+"F0.wireOp",EDGE,"E29.trimOffspring"),sQuery(id+"F0.wireOp",EDGE,"E30.trimOffspring"),sQuery(id+"F0.wireOp",EDGE,"E31.trimOffspring"),sQuery(id+"F0.wireOp",EDGE,"E32.trimOffspring"),sQuery(id+"F0.wireOp",EDGE,"E33.trimOffspring"),sQuery(id+"F0.wireOp",EDGE,"E34.trimOffspring"),sQuery(id+"F0.wireOp",EDGE,"E35.trimOffspring"),sQuery(id+"F0.wireOp",EDGE,"E36.trimOffspring"),sQuery(id+"F0.wireOp",EDGE,"E37.trimOffspring"),sQuery(id+"F0.wireOp",EDGE,"E38.trimOffspring"),sQuery(id+"F0.wireOp",EDGE,"E39.trimOffspring"),sQuery(id+"F0.wireOp",EDGE,"E40.trimOffspring"),sQuery(id+"F0.wireOp",EDGE,"E41.trimOffspring"),sQuery(id+"F0.wireOp",EDGE,"E42.trimOffspring"),sQuery(id+"F0.wireOp",EDGE,"E43.trimOffspring"),sQuery(id+"F0.wireOp",EDGE,"E44.trimOffspring"),sQuery(id+"F0.wireOp",EDGE,"E45.trimOffspring"),sQuery(id+"F0.wireOp",EDGE,"E46.trimOffspring"),sQuery(id+"F0.wireOp",EDGE,"E47.trimOffspring"),sQuery(id+"F0.wireOp",EDGE,"E48.trimOffspring")])],"isStart":false});
            var sketch = newSketch(context, id + "F2", { "sketchPlane" : qUnion([Q0])});
            skPoint(sketch, "E49", {"position": v(0, 0) * mm});
            skSolve(sketch);
        }
        {
            var Q0;
            Q0=sQuery(id+"F2.wireOp",VERTEX,"E49");
            var Q1;
            Q1=makeQuery(id+"F1.opExtrude","SWEPT_BODY",BODY,{"disambiguationData":[OSD([sQuery(id+"F0.wireOp",EDGE,"E0"),sQuery(id+"F0.wireOp",EDGE,"E1.trimOffspring"),sQuery(id+"F0.wireOp",EDGE,"E2"),sQuery(id+"F0.wireOp",EDGE,"E3"),sQuery(id+"F0.wireOp",EDGE,"E4.MirrorCS"),sQuery(id+"F0.wireOp",EDGE,"E5.MirrorCS"),sQuery(id+"F0.wireOp",EDGE,"E6.MirrorCS"),sQuery(id+"F0.wireOp",EDGE,"E7.filletArc"),sQuery(id+"F0.wireOp",EDGE,"E8.filletArc"),sQuery(id+"F0.wireOp",EDGE,"E9.filletArc"),sQuery(id+"F0.wireOp",EDGE,"E10.filletArc"),sQuery(id+"F0.wireOp",EDGE,"E11.filletArc"),sQuery(id+"F0.wireOp",EDGE,"E12.filletArc"),sQuery(id+"F0.wireOp",EDGE,"E13.1.0"),sQuery(id+"F0.wireOp",EDGE,"E13.1.1"),sQuery(id+"F0.wireOp",EDGE,"E13.1.2"),sQuery(id+"F0.wireOp",EDGE,"E13.1.3"),sQuery(id+"F0.wireOp",EDGE,"E13.1.4"),sQuery(id+"F0.wireOp",EDGE,"E13.1.5"),sQuery(id+"F0.wireOp",EDGE,"E13.1.6"),sQuery(id+"F0.wireOp",EDGE,"E13.1.7"),sQuery(id+"F0.wireOp",EDGE,"E13.1.8"),sQuery(id+"F0.wireOp",EDGE,"E13.1.9"),sQuery(id+"F0.wireOp",EDGE,"E13.1.10"),sQuery(id+"F0.wireOp",EDGE,"E13.1.11"),sQuery(id+"F0.wireOp",EDGE,"E13.2.0"),sQuery(id+"F0.wireOp",EDGE,"E13.2.1"),sQuery(id+"F0.wireOp",EDGE,"E13.2.2"),sQuery(id+"F0.wireOp",EDGE,"E13.2.3"),sQuery(id+"F0.wireOp",EDGE,"E13.2.4"),sQuery(id+"F0.wireOp",EDGE,"E13.2.5"),sQuery(id+"F0.wireOp",EDGE,"E13.2.6"),sQuery(id+"F0.wireOp",EDGE,"E13.2.7"),sQuery(id+"F0.wireOp",EDGE,"E13.2.8"),sQuery(id+"F0.wireOp",EDGE,"E13.2.9"),sQuery(id+"F0.wireOp",EDGE,"E13.2.10"),sQuery(id+"F0.wireOp",EDGE,"E13.2.11"),sQuery(id+"F0.wireOp",EDGE,"E13.3.0"),sQuery(id+"F0.wireOp",EDGE,"E13.3.1"),sQuery(id+"F0.wireOp",EDGE,"E13.3.2"),sQuery(id+"F0.wireOp",EDGE,"E13.3.3"),sQuery(id+"F0.wireOp",EDGE,"E13.3.4"),sQuery(id+"F0.wireOp",EDGE,"E13.3.5"),sQuery(id+"F0.wireOp",EDGE,"E13.3.6"),sQuery(id+"F0.wireOp",EDGE,"E13.3.7"),sQuery(id+"F0.wireOp",EDGE,"E13.3.8"),sQuery(id+"F0.wireOp",EDGE,"E13.3.9"),sQuery(id+"F0.wireOp",EDGE,"E13.3.10"),sQuery(id+"F0.wireOp",EDGE,"E13.3.11"),sQuery(id+"F0.wireOp",EDGE,"E13.4.0"),sQuery(id+"F0.wireOp",EDGE,"E13.4.1"),sQuery(id+"F0.wireOp",EDGE,"E13.4.2"),sQuery(id+"F0.wireOp",EDGE,"E13.4.3"),sQuery(id+"F0.wireOp",EDGE,"E13.4.4"),sQuery(id+"F0.wireOp",EDGE,"E13.4.5"),sQuery(id+"F0.wireOp",EDGE,"E13.4.6"),sQuery(id+"F0.wireOp",EDGE,"E13.4.7"),sQuery(id+"F0.wireOp",EDGE,"E13.4.8"),sQuery(id+"F0.wireOp",EDGE,"E13.4.9"),sQuery(id+"F0.wireOp",EDGE,"E13.4.10"),sQuery(id+"F0.wireOp",EDGE,"E13.4.11"),sQuery(id+"F0.wireOp",EDGE,"E13.5.0"),sQuery(id+"F0.wireOp",EDGE,"E13.5.1"),sQuery(id+"F0.wireOp",EDGE,"E13.5.2"),sQuery(id+"F0.wireOp",EDGE,"E13.5.3"),sQuery(id+"F0.wireOp",EDGE,"E13.5.4"),sQuery(id+"F0.wireOp",EDGE,"E13.5.5"),sQuery(id+"F0.wireOp",EDGE,"E13.5.6"),sQuery(id+"F0.wireOp",EDGE,"E13.5.7"),sQuery(id+"F0.wireOp",EDGE,"E13.5.8"),sQuery(id+"F0.wireOp",EDGE,"E13.5.9"),sQuery(id+"F0.wireOp",EDGE,"E13.5.10"),sQuery(id+"F0.wireOp",EDGE,"E13.5.11"),sQuery(id+"F0.wireOp",EDGE,"E13.6.0"),sQuery(id+"F0.wireOp",EDGE,"E13.6.1"),sQuery(id+"F0.wireOp",EDGE,"E13.6.2"),sQuery(id+"F0.wireOp",EDGE,"E13.6.3"),sQuery(id+"F0.wireOp",EDGE,"E13.6.4"),sQuery(id+"F0.wireOp",EDGE,"E13.6.5"),sQuery(id+"F0.wireOp",EDGE,"E13.6.6"),sQuery(id+"F0.wireOp",EDGE,"E13.6.7"),sQuery(id+"F0.wireOp",EDGE,"E13.6.8"),sQuery(id+"F0.wireOp",EDGE,"E13.6.9"),sQuery(id+"F0.wireOp",EDGE,"E13.6.10"),sQuery(id+"F0.wireOp",EDGE,"E13.6.11"),sQuery(id+"F0.wireOp",EDGE,"E13.7.0"),sQuery(id+"F0.wireOp",EDGE,"E13.7.1"),sQuery(id+"F0.wireOp",EDGE,"E13.7.2"),sQuery(id+"F0.wireOp",EDGE,"E13.7.3"),sQuery(id+"F0.wireOp",EDGE,"E13.7.4"),sQuery(id+"F0.wireOp",EDGE,"E13.7.5"),sQuery(id+"F0.wireOp",EDGE,"E13.7.6"),sQuery(id+"F0.wireOp",EDGE,"E13.7.7"),sQuery(id+"F0.wireOp",EDGE,"E13.7.8"),sQuery(id+"F0.wireOp",EDGE,"E13.7.9"),sQuery(id+"F0.wireOp",EDGE,"E13.7.10"),sQuery(id+"F0.wireOp",EDGE,"E13.7.11"),sQuery(id+"F0.wireOp",EDGE,"E13.8.0"),sQuery(id+"F0.wireOp",EDGE,"E13.8.1"),sQuery(id+"F0.wireOp",EDGE,"E13.8.2"),sQuery(id+"F0.wireOp",EDGE,"E13.8.3"),sQuery(id+"F0.wireOp",EDGE,"E13.8.4"),sQuery(id+"F0.wireOp",EDGE,"E13.8.5"),sQuery(id+"F0.wireOp",EDGE,"E13.8.6"),sQuery(id+"F0.wireOp",EDGE,"E13.8.7"),sQuery(id+"F0.wireOp",EDGE,"E13.8.8"),sQuery(id+"F0.wireOp",EDGE,"E13.8.9"),sQuery(id+"F0.wireOp",EDGE,"E13.8.10"),sQuery(id+"F0.wireOp",EDGE,"E13.8.11"),sQuery(id+"F0.wireOp",EDGE,"E13.9.0"),sQuery(id+"F0.wireOp",EDGE,"E13.9.1"),sQuery(id+"F0.wireOp",EDGE,"E13.9.2"),sQuery(id+"F0.wireOp",EDGE,"E13.9.3"),sQuery(id+"F0.wireOp",EDGE,"E13.9.4"),sQuery(id+"F0.wireOp",EDGE,"E13.9.5"),sQuery(id+"F0.wireOp",EDGE,"E13.9.6"),sQuery(id+"F0.wireOp",EDGE,"E13.9.7"),sQuery(id+"F0.wireOp",EDGE,"E13.9.8"),sQuery(id+"F0.wireOp",EDGE,"E13.9.9"),sQuery(id+"F0.wireOp",EDGE,"E13.9.10"),sQuery(id+"F0.wireOp",EDGE,"E13.9.11"),sQuery(id+"F0.wireOp",EDGE,"E13.10.0"),sQuery(id+"F0.wireOp",EDGE,"E13.10.1"),sQuery(id+"F0.wireOp",EDGE,"E13.10.2"),sQuery(id+"F0.wireOp",EDGE,"E13.10.3"),sQuery(id+"F0.wireOp",EDGE,"E13.10.4"),sQuery(id+"F0.wireOp",EDGE,"E13.10.5"),sQuery(id+"F0.wireOp",EDGE,"E13.10.6"),sQuery(id+"F0.wireOp",EDGE,"E13.10.7"),sQuery(id+"F0.wireOp",EDGE,"E13.10.8"),sQuery(id+"F0.wireOp",EDGE,"E13.10.9"),sQuery(id+"F0.wireOp",EDGE,"E13.10.10"),sQuery(id+"F0.wireOp",EDGE,"E13.10.11"),sQuery(id+"F0.wireOp",EDGE,"E13.11.0"),sQuery(id+"F0.wireOp",EDGE,"E13.11.1"),sQuery(id+"F0.wireOp",EDGE,"E13.11.2"),sQuery(id+"F0.wireOp",EDGE,"E13.11.3"),sQuery(id+"F0.wireOp",EDGE,"E13.11.4"),sQuery(id+"F0.wireOp",EDGE,"E13.11.5"),sQuery(id+"F0.wireOp",EDGE,"E13.11.6"),sQuery(id+"F0.wireOp",EDGE,"E13.11.7"),sQuery(id+"F0.wireOp",EDGE,"E13.11.8"),sQuery(id+"F0.wireOp",EDGE,"E13.11.9"),sQuery(id+"F0.wireOp",EDGE,"E13.11.10"),sQuery(id+"F0.wireOp",EDGE,"E13.11.11"),sQuery(id+"F0.wireOp",EDGE,"E13.12.0"),sQuery(id+"F0.wireOp",EDGE,"E13.12.1"),sQuery(id+"F0.wireOp",EDGE,"E13.12.2"),sQuery(id+"F0.wireOp",EDGE,"E13.12.3"),sQuery(id+"F0.wireOp",EDGE,"E13.12.4"),sQuery(id+"F0.wireOp",EDGE,"E13.12.5"),sQuery(id+"F0.wireOp",EDGE,"E13.12.6"),sQuery(id+"F0.wireOp",EDGE,"E13.12.7"),sQuery(id+"F0.wireOp",EDGE,"E13.12.8"),sQuery(id+"F0.wireOp",EDGE,"E13.12.9"),sQuery(id+"F0.wireOp",EDGE,"E13.12.10"),sQuery(id+"F0.wireOp",EDGE,"E13.12.11"),sQuery(id+"F0.wireOp",EDGE,"E13.13.0"),sQuery(id+"F0.wireOp",EDGE,"E13.13.1"),sQuery(id+"F0.wireOp",EDGE,"E13.13.2"),sQuery(id+"F0.wireOp",EDGE,"E13.13.3"),sQuery(id+"F0.wireOp",EDGE,"E13.13.4"),sQuery(id+"F0.wireOp",EDGE,"E13.13.5"),sQuery(id+"F0.wireOp",EDGE,"E13.13.6"),sQuery(id+"F0.wireOp",EDGE,"E13.13.7"),sQuery(id+"F0.wireOp",EDGE,"E13.13.8"),sQuery(id+"F0.wireOp",EDGE,"E13.13.9"),sQuery(id+"F0.wireOp",EDGE,"E13.13.10"),sQuery(id+"F0.wireOp",EDGE,"E13.13.11"),sQuery(id+"F0.wireOp",EDGE,"E13.14.0"),sQuery(id+"F0.wireOp",EDGE,"E13.14.1"),sQuery(id+"F0.wireOp",EDGE,"E13.14.2"),sQuery(id+"F0.wireOp",EDGE,"E13.14.3"),sQuery(id+"F0.wireOp",EDGE,"E13.14.4"),sQuery(id+"F0.wireOp",EDGE,"E13.14.5"),sQuery(id+"F0.wireOp",EDGE,"E13.14.6"),sQuery(id+"F0.wireOp",EDGE,"E13.14.7"),sQuery(id+"F0.wireOp",EDGE,"E13.14.8"),sQuery(id+"F0.wireOp",EDGE,"E13.14.9"),sQuery(id+"F0.wireOp",EDGE,"E13.14.10"),sQuery(id+"F0.wireOp",EDGE,"E13.14.11"),sQuery(id+"F0.wireOp",EDGE,"E13.15.0"),sQuery(id+"F0.wireOp",EDGE,"E13.15.1"),sQuery(id+"F0.wireOp",EDGE,"E13.15.2"),sQuery(id+"F0.wireOp",EDGE,"E13.15.3"),sQuery(id+"F0.wireOp",EDGE,"E13.15.4"),sQuery(id+"F0.wireOp",EDGE,"E13.15.5"),sQuery(id+"F0.wireOp",EDGE,"E13.15.6"),sQuery(id+"F0.wireOp",EDGE,"E13.15.7"),sQuery(id+"F0.wireOp",EDGE,"E13.15.8"),sQuery(id+"F0.wireOp",EDGE,"E13.15.9"),sQuery(id+"F0.wireOp",EDGE,"E13.15.10"),sQuery(id+"F0.wireOp",EDGE,"E13.15.11"),sQuery(id+"F0.wireOp",EDGE,"E13.16.0"),sQuery(id+"F0.wireOp",EDGE,"E13.16.1"),sQuery(id+"F0.wireOp",EDGE,"E13.16.2"),sQuery(id+"F0.wireOp",EDGE,"E13.16.3"),sQuery(id+"F0.wireOp",EDGE,"E13.16.4"),sQuery(id+"F0.wireOp",EDGE,"E13.16.5"),sQuery(id+"F0.wireOp",EDGE,"E13.16.6"),sQuery(id+"F0.wireOp",EDGE,"E13.16.7"),sQuery(id+"F0.wireOp",EDGE,"E13.16.8"),sQuery(id+"F0.wireOp",EDGE,"E13.16.9"),sQuery(id+"F0.wireOp",EDGE,"E13.16.10"),sQuery(id+"F0.wireOp",EDGE,"E13.16.11"),sQuery(id+"F0.wireOp",EDGE,"E13.17.0"),sQuery(id+"F0.wireOp",EDGE,"E13.17.1"),sQuery(id+"F0.wireOp",EDGE,"E13.17.2"),sQuery(id+"F0.wireOp",EDGE,"E13.17.3"),sQuery(id+"F0.wireOp",EDGE,"E13.17.4"),sQuery(id+"F0.wireOp",EDGE,"E13.17.5"),sQuery(id+"F0.wireOp",EDGE,"E13.17.6"),sQuery(id+"F0.wireOp",EDGE,"E13.17.7"),sQuery(id+"F0.wireOp",EDGE,"E13.17.8"),sQuery(id+"F0.wireOp",EDGE,"E13.17.9"),sQuery(id+"F0.wireOp",EDGE,"E13.17.10"),sQuery(id+"F0.wireOp",EDGE,"E13.17.11"),sQuery(id+"F0.wireOp",EDGE,"E13.18.0"),sQuery(id+"F0.wireOp",EDGE,"E13.18.1"),sQuery(id+"F0.wireOp",EDGE,"E13.18.2"),sQuery(id+"F0.wireOp",EDGE,"E13.18.3"),sQuery(id+"F0.wireOp",EDGE,"E13.18.4"),sQuery(id+"F0.wireOp",EDGE,"E13.18.5"),sQuery(id+"F0.wireOp",EDGE,"E13.18.6"),sQuery(id+"F0.wireOp",EDGE,"E13.18.7"),sQuery(id+"F0.wireOp",EDGE,"E13.18.8"),sQuery(id+"F0.wireOp",EDGE,"E13.18.9"),sQuery(id+"F0.wireOp",EDGE,"E13.18.10"),sQuery(id+"F0.wireOp",EDGE,"E13.18.11"),sQuery(id+"F0.wireOp",EDGE,"E13.19.0"),sQuery(id+"F0.wireOp",EDGE,"E13.19.1"),sQuery(id+"F0.wireOp",EDGE,"E13.19.2"),sQuery(id+"F0.wireOp",EDGE,"E13.19.3"),sQuery(id+"F0.wireOp",EDGE,"E13.19.4"),sQuery(id+"F0.wireOp",EDGE,"E13.19.5"),sQuery(id+"F0.wireOp",EDGE,"E13.19.6"),sQuery(id+"F0.wireOp",EDGE,"E13.19.7"),sQuery(id+"F0.wireOp",EDGE,"E13.19.8"),sQuery(id+"F0.wireOp",EDGE,"E13.19.9"),sQuery(id+"F0.wireOp",EDGE,"E13.19.10"),sQuery(id+"F0.wireOp",EDGE,"E13.19.11"),sQuery(id+"F0.wireOp",EDGE,"E13.20.0"),sQuery(id+"F0.wireOp",EDGE,"E13.20.1"),sQuery(id+"F0.wireOp",EDGE,"E13.20.2"),sQuery(id+"F0.wireOp",EDGE,"E13.20.3"),sQuery(id+"F0.wireOp",EDGE,"E13.20.4"),sQuery(id+"F0.wireOp",EDGE,"E13.20.5"),sQuery(id+"F0.wireOp",EDGE,"E13.20.6"),sQuery(id+"F0.wireOp",EDGE,"E13.20.7"),sQuery(id+"F0.wireOp",EDGE,"E13.20.8"),sQuery(id+"F0.wireOp",EDGE,"E13.20.9"),sQuery(id+"F0.wireOp",EDGE,"E13.20.10"),sQuery(id+"F0.wireOp",EDGE,"E13.20.11"),sQuery(id+"F0.wireOp",EDGE,"E13.21.0"),sQuery(id+"F0.wireOp",EDGE,"E13.21.1"),sQuery(id+"F0.wireOp",EDGE,"E13.21.2"),sQuery(id+"F0.wireOp",EDGE,"E13.21.3"),sQuery(id+"F0.wireOp",EDGE,"E13.21.4"),sQuery(id+"F0.wireOp",EDGE,"E13.21.5"),sQuery(id+"F0.wireOp",EDGE,"E13.21.6"),sQuery(id+"F0.wireOp",EDGE,"E13.21.7"),sQuery(id+"F0.wireOp",EDGE,"E13.21.8"),sQuery(id+"F0.wireOp",EDGE,"E13.21.9"),sQuery(id+"F0.wireOp",EDGE,"E13.21.10"),sQuery(id+"F0.wireOp",EDGE,"E13.21.11"),sQuery(id+"F0.wireOp",EDGE,"E13.22.0"),sQuery(id+"F0.wireOp",EDGE,"E13.22.1"),sQuery(id+"F0.wireOp",EDGE,"E13.22.2"),sQuery(id+"F0.wireOp",EDGE,"E13.22.3"),sQuery(id+"F0.wireOp",EDGE,"E13.22.4"),sQuery(id+"F0.wireOp",EDGE,"E13.22.5"),sQuery(id+"F0.wireOp",EDGE,"E13.22.6"),sQuery(id+"F0.wireOp",EDGE,"E13.22.7"),sQuery(id+"F0.wireOp",EDGE,"E13.22.8"),sQuery(id+"F0.wireOp",EDGE,"E13.22.9"),sQuery(id+"F0.wireOp",EDGE,"E13.22.10"),sQuery(id+"F0.wireOp",EDGE,"E13.22.11"),sQuery(id+"F0.wireOp",EDGE,"E13.23.0"),sQuery(id+"F0.wireOp",EDGE,"E13.23.1"),sQuery(id+"F0.wireOp",EDGE,"E13.23.2"),sQuery(id+"F0.wireOp",EDGE,"E13.23.3"),sQuery(id+"F0.wireOp",EDGE,"E13.23.4"),sQuery(id+"F0.wireOp",EDGE,"E13.23.5"),sQuery(id+"F0.wireOp",EDGE,"E13.23.6"),sQuery(id+"F0.wireOp",EDGE,"E13.23.7"),sQuery(id+"F0.wireOp",EDGE,"E13.23.8"),sQuery(id+"F0.wireOp",EDGE,"E13.23.9"),sQuery(id+"F0.wireOp",EDGE,"E13.23.10"),sQuery(id+"F0.wireOp",EDGE,"E13.23.11"),sQuery(id+"F0.wireOp",EDGE,"E13.24.0"),sQuery(id+"F0.wireOp",EDGE,"E13.24.1"),sQuery(id+"F0.wireOp",EDGE,"E13.24.2"),sQuery(id+"F0.wireOp",EDGE,"E13.24.3"),sQuery(id+"F0.wireOp",EDGE,"E13.24.4"),sQuery(id+"F0.wireOp",EDGE,"E13.24.5"),sQuery(id+"F0.wireOp",EDGE,"E13.24.6"),sQuery(id+"F0.wireOp",EDGE,"E13.24.7"),sQuery(id+"F0.wireOp",EDGE,"E13.24.8"),sQuery(id+"F0.wireOp",EDGE,"E13.24.9"),sQuery(id+"F0.wireOp",EDGE,"E13.24.10"),sQuery(id+"F0.wireOp",EDGE,"E13.24.11"),sQuery(id+"F0.wireOp",EDGE,"E13.25.0"),sQuery(id+"F0.wireOp",EDGE,"E13.25.1"),sQuery(id+"F0.wireOp",EDGE,"E13.25.2"),sQuery(id+"F0.wireOp",EDGE,"E13.25.3"),sQuery(id+"F0.wireOp",EDGE,"E13.25.4"),sQuery(id+"F0.wireOp",EDGE,"E13.25.5"),sQuery(id+"F0.wireOp",EDGE,"E13.25.6"),sQuery(id+"F0.wireOp",EDGE,"E13.25.7"),sQuery(id+"F0.wireOp",EDGE,"E13.25.8"),sQuery(id+"F0.wireOp",EDGE,"E13.25.9"),sQuery(id+"F0.wireOp",EDGE,"E13.25.10"),sQuery(id+"F0.wireOp",EDGE,"E13.25.11"),sQuery(id+"F0.wireOp",EDGE,"E13.26.0"),sQuery(id+"F0.wireOp",EDGE,"E13.26.1"),sQuery(id+"F0.wireOp",EDGE,"E13.26.2"),sQuery(id+"F0.wireOp",EDGE,"E13.26.3"),sQuery(id+"F0.wireOp",EDGE,"E13.26.4"),sQuery(id+"F0.wireOp",EDGE,"E13.26.5"),sQuery(id+"F0.wireOp",EDGE,"E13.26.6"),sQuery(id+"F0.wireOp",EDGE,"E13.26.7"),sQuery(id+"F0.wireOp",EDGE,"E13.26.8"),sQuery(id+"F0.wireOp",EDGE,"E13.26.9"),sQuery(id+"F0.wireOp",EDGE,"E13.26.10"),sQuery(id+"F0.wireOp",EDGE,"E13.26.11"),sQuery(id+"F0.wireOp",EDGE,"E13.27.0"),sQuery(id+"F0.wireOp",EDGE,"E13.27.1"),sQuery(id+"F0.wireOp",EDGE,"E13.27.2"),sQuery(id+"F0.wireOp",EDGE,"E13.27.3"),sQuery(id+"F0.wireOp",EDGE,"E13.27.4"),sQuery(id+"F0.wireOp",EDGE,"E13.27.5"),sQuery(id+"F0.wireOp",EDGE,"E13.27.6"),sQuery(id+"F0.wireOp",EDGE,"E13.27.7"),sQuery(id+"F0.wireOp",EDGE,"E13.27.8"),sQuery(id+"F0.wireOp",EDGE,"E13.27.9"),sQuery(id+"F0.wireOp",EDGE,"E13.27.10"),sQuery(id+"F0.wireOp",EDGE,"E13.27.11"),sQuery(id+"F0.wireOp",EDGE,"E13.28.0"),sQuery(id+"F0.wireOp",EDGE,"E13.28.1"),sQuery(id+"F0.wireOp",EDGE,"E13.28.2"),sQuery(id+"F0.wireOp",EDGE,"E13.28.3"),sQuery(id+"F0.wireOp",EDGE,"E13.28.4"),sQuery(id+"F0.wireOp",EDGE,"E13.28.5"),sQuery(id+"F0.wireOp",EDGE,"E13.28.6"),sQuery(id+"F0.wireOp",EDGE,"E13.28.7"),sQuery(id+"F0.wireOp",EDGE,"E13.28.8"),sQuery(id+"F0.wireOp",EDGE,"E13.28.9"),sQuery(id+"F0.wireOp",EDGE,"E13.28.10"),sQuery(id+"F0.wireOp",EDGE,"E13.28.11"),sQuery(id+"F0.wireOp",EDGE,"E13.29.0"),sQuery(id+"F0.wireOp",EDGE,"E13.29.1"),sQuery(id+"F0.wireOp",EDGE,"E13.29.2"),sQuery(id+"F0.wireOp",EDGE,"E13.29.3"),sQuery(id+"F0.wireOp",EDGE,"E13.29.4"),sQuery(id+"F0.wireOp",EDGE,"E13.29.5"),sQuery(id+"F0.wireOp",EDGE,"E13.29.6"),sQuery(id+"F0.wireOp",EDGE,"E13.29.7"),sQuery(id+"F0.wireOp",EDGE,"E13.29.8"),sQuery(id+"F0.wireOp",EDGE,"E13.29.9"),sQuery(id+"F0.wireOp",EDGE,"E13.29.10"),sQuery(id+"F0.wireOp",EDGE,"E13.29.11"),sQuery(id+"F0.wireOp",EDGE,"E13.30.0"),sQuery(id+"F0.wireOp",EDGE,"E13.30.1"),sQuery(id+"F0.wireOp",EDGE,"E13.30.2"),sQuery(id+"F0.wireOp",EDGE,"E13.30.3"),sQuery(id+"F0.wireOp",EDGE,"E13.30.4"),sQuery(id+"F0.wireOp",EDGE,"E13.30.5"),sQuery(id+"F0.wireOp",EDGE,"E13.30.6"),sQuery(id+"F0.wireOp",EDGE,"E13.30.7"),sQuery(id+"F0.wireOp",EDGE,"E13.30.8"),sQuery(id+"F0.wireOp",EDGE,"E13.30.9"),sQuery(id+"F0.wireOp",EDGE,"E13.30.10"),sQuery(id+"F0.wireOp",EDGE,"E13.30.11"),sQuery(id+"F0.wireOp",EDGE,"E13.31.0"),sQuery(id+"F0.wireOp",EDGE,"E13.31.1"),sQuery(id+"F0.wireOp",EDGE,"E13.31.2"),sQuery(id+"F0.wireOp",EDGE,"E13.31.3"),sQuery(id+"F0.wireOp",EDGE,"E13.31.4"),sQuery(id+"F0.wireOp",EDGE,"E13.31.5"),sQuery(id+"F0.wireOp",EDGE,"E13.31.6"),sQuery(id+"F0.wireOp",EDGE,"E13.31.7"),sQuery(id+"F0.wireOp",EDGE,"E13.31.8"),sQuery(id+"F0.wireOp",EDGE,"E13.31.9"),sQuery(id+"F0.wireOp",EDGE,"E13.31.10"),sQuery(id+"F0.wireOp",EDGE,"E13.31.11"),sQuery(id+"F0.wireOp",EDGE,"E13.32.0"),sQuery(id+"F0.wireOp",EDGE,"E13.32.1"),sQuery(id+"F0.wireOp",EDGE,"E13.32.2"),sQuery(id+"F0.wireOp",EDGE,"E13.32.3"),sQuery(id+"F0.wireOp",EDGE,"E13.32.4"),sQuery(id+"F0.wireOp",EDGE,"E13.32.5"),sQuery(id+"F0.wireOp",EDGE,"E13.32.6"),sQuery(id+"F0.wireOp",EDGE,"E13.32.7"),sQuery(id+"F0.wireOp",EDGE,"E13.32.8"),sQuery(id+"F0.wireOp",EDGE,"E13.32.9"),sQuery(id+"F0.wireOp",EDGE,"E13.32.10"),sQuery(id+"F0.wireOp",EDGE,"E13.32.11"),sQuery(id+"F0.wireOp",EDGE,"E13.33.0"),sQuery(id+"F0.wireOp",EDGE,"E13.33.1"),sQuery(id+"F0.wireOp",EDGE,"E13.33.2"),sQuery(id+"F0.wireOp",EDGE,"E13.33.3"),sQuery(id+"F0.wireOp",EDGE,"E13.33.4"),sQuery(id+"F0.wireOp",EDGE,"E13.33.5"),sQuery(id+"F0.wireOp",EDGE,"E13.33.6"),sQuery(id+"F0.wireOp",EDGE,"E13.33.7"),sQuery(id+"F0.wireOp",EDGE,"E13.33.8"),sQuery(id+"F0.wireOp",EDGE,"E13.33.9"),sQuery(id+"F0.wireOp",EDGE,"E13.33.10"),sQuery(id+"F0.wireOp",EDGE,"E13.33.11"),sQuery(id+"F0.wireOp",EDGE,"E13.34.0"),sQuery(id+"F0.wireOp",EDGE,"E13.34.1"),sQuery(id+"F0.wireOp",EDGE,"E13.34.2"),sQuery(id+"F0.wireOp",EDGE,"E13.34.3"),sQuery(id+"F0.wireOp",EDGE,"E13.34.4"),sQuery(id+"F0.wireOp",EDGE,"E13.34.5"),sQuery(id+"F0.wireOp",EDGE,"E13.34.6"),sQuery(id+"F0.wireOp",EDGE,"E13.34.7"),sQuery(id+"F0.wireOp",EDGE,"E13.34.8"),sQuery(id+"F0.wireOp",EDGE,"E13.34.9"),sQuery(id+"F0.wireOp",EDGE,"E13.34.10"),sQuery(id+"F0.wireOp",EDGE,"E13.34.11"),sQuery(id+"F0.wireOp",EDGE,"E13.35.0"),sQuery(id+"F0.wireOp",EDGE,"E13.35.1"),sQuery(id+"F0.wireOp",EDGE,"E13.35.2"),sQuery(id+"F0.wireOp",EDGE,"E13.35.3"),sQuery(id+"F0.wireOp",EDGE,"E13.35.4"),sQuery(id+"F0.wireOp",EDGE,"E13.35.5"),sQuery(id+"F0.wireOp",EDGE,"E13.35.6"),sQuery(id+"F0.wireOp",EDGE,"E13.35.7"),sQuery(id+"F0.wireOp",EDGE,"E13.35.8"),sQuery(id+"F0.wireOp",EDGE,"E13.35.9"),sQuery(id+"F0.wireOp",EDGE,"E13.35.10"),sQuery(id+"F0.wireOp",EDGE,"E13.35.11"),sQuery(id+"F0.wireOp",EDGE,"E14.trimOffspring"),sQuery(id+"F0.wireOp",EDGE,"E15.trimOffspring"),sQuery(id+"F0.wireOp",EDGE,"E16.trimOffspring"),sQuery(id+"F0.wireOp",EDGE,"E17.trimOffspring"),sQuery(id+"F0.wireOp",EDGE,"E18.trimOffspring"),sQuery(id+"F0.wireOp",EDGE,"E19.trimOffspring"),sQuery(id+"F0.wireOp",EDGE,"E20.trimOffspring"),sQuery(id+"F0.wireOp",EDGE,"E21.trimOffspring"),sQuery(id+"F0.wireOp",EDGE,"E22.trimOffspring"),sQuery(id+"F0.wireOp",EDGE,"E23.trimOffspring"),sQuery(id+"F0.wireOp",EDGE,"E24.trimOffspring"),sQuery(id+"F0.wireOp",EDGE,"E25.trimOffspring"),sQuery(id+"F0.wireOp",EDGE,"E26.trimOffspring"),sQuery(id+"F0.wireOp",EDGE,"E27.trimOffspring"),sQuery(id+"F0.wireOp",EDGE,"E28.trimOffspring"),sQuery(id+"F0.wireOp",EDGE,"E29.trimOffspring"),sQuery(id+"F0.wireOp",EDGE,"E30.trimOffspring"),sQuery(id+"F0.wireOp",EDGE,"E31.trimOffspring"),sQuery(id+"F0.wireOp",EDGE,"E32.trimOffspring"),sQuery(id+"F0.wireOp",EDGE,"E33.trimOffspring"),sQuery(id+"F0.wireOp",EDGE,"E34.trimOffspring"),sQuery(id+"F0.wireOp",EDGE,"E35.trimOffspring"),sQuery(id+"F0.wireOp",EDGE,"E36.trimOffspring"),sQuery(id+"F0.wireOp",EDGE,"E37.trimOffspring"),sQuery(id+"F0.wireOp",EDGE,"E38.trimOffspring"),sQuery(id+"F0.wireOp",EDGE,"E39.trimOffspring"),sQuery(id+"F0.wireOp",EDGE,"E40.trimOffspring"),sQuery(id+"F0.wireOp",EDGE,"E41.trimOffspring"),sQuery(id+"F0.wireOp",EDGE,"E42.trimOffspring"),sQuery(id+"F0.wireOp",EDGE,"E43.trimOffspring"),sQuery(id+"F0.wireOp",EDGE,"E44.trimOffspring"),sQuery(id+"F0.wireOp",EDGE,"E45.trimOffspring"),sQuery(id+"F0.wireOp",EDGE,"E46.trimOffspring"),sQuery(id+"F0.wireOp",EDGE,"E47.trimOffspring"),sQuery(id+"F0.wireOp",EDGE,"E48.trimOffspring")])]});
            hole(context, id + "F3", {"style" : HoleStyle.SIMPLE, "endStyle" : HoleEndStyle.THROUGH, "holeDiameter" : 12.7 * mm, "tappedDepth" : 12.7 * mm, "tapClearance" : 3, "locations" : qUnion([Q0]), "scope" : qUnion([Q1])});
        }
    });
